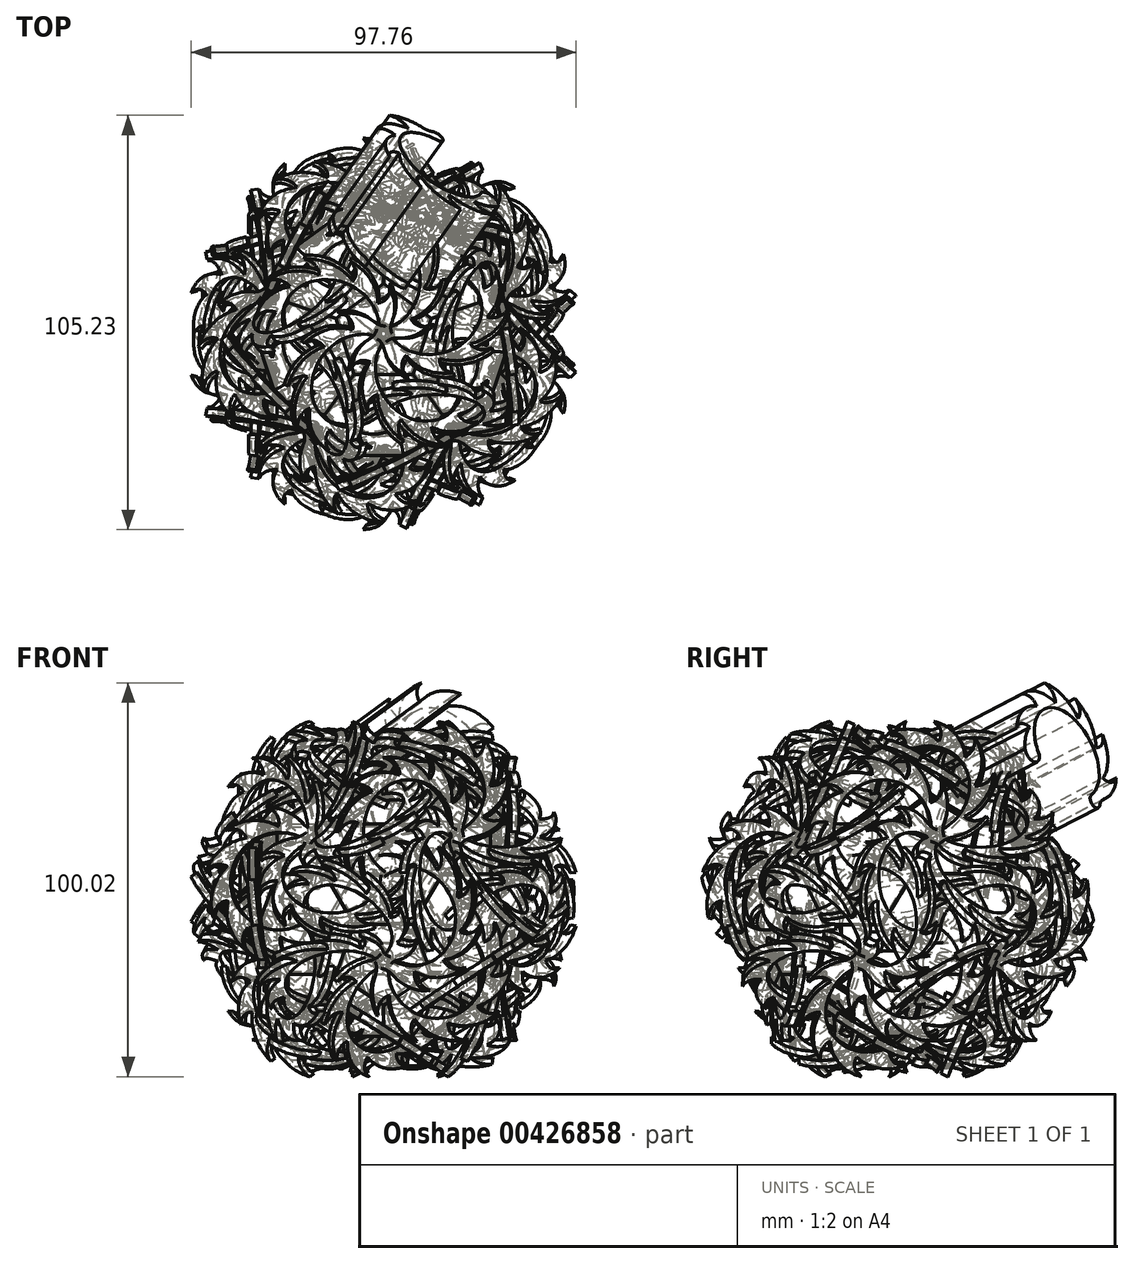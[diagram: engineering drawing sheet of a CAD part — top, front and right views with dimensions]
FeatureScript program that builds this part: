
annotation { "Feature Type Name" : "Feature", "Feature Type Description" : "" }
export const myFeature = defineFeature(function(context is Context, id is Id, definition is map)
    precondition{}
    {
        {
            var Q0;
            Q0=qCreatedBy(makeId("Top.planeOp"),FACE);
            var sketch = newSketch(context, id + "F0", { "sketchPlane" : qUnion([Q0])});
            skCircle(sketch, "E0.cCircle", {"center": v(0, 0) * mm, "radius": 10.32 * mm, "construction": true});
            skLineSegment(sketch, "E0.0", {"start": v(7.5, -10.32) * mm, "end": v(-7.5, -10.32) * mm});
            skLineSegment(sketch, "E0.1", {"start": v(-7.5, -10.32) * mm, "end": v(-12.14, 3.94) * mm});
            skLineSegment(sketch, "E0.2", {"start": v(-12.14, 3.94) * mm, "end": v(0, 12.76) * mm});
            skLineSegment(sketch, "E0.3", {"start": v(0, 12.76) * mm, "end": v(12.14, 3.94) * mm});
            skLineSegment(sketch, "E0.4", {"start": v(12.14, 3.94) * mm, "end": v(7.5, -10.32) * mm});
            skPoint(sketch, "E0.0.midPoint", {"position": v(0, -10.32) * mm});
            skLineSegment(sketch, "E1", {"start": v(0, 12.76) * mm, "end": v(0, -10.32) * mm});
            skSolve(sketch);
        }
        {
            var Q0;
            Q0=qCreatedBy(makeId("Top.planeOp"),FACE);
            var sketch = newSketch(context, id + "F1", { "sketchPlane" : qUnion([Q0])});
            skCircle(sketch, "E2.cCircle", {"center": v(22.17, -7.2) * mm, "radius": 13 * mm, "construction": true});
            skLineSegment(sketch, "E2.0", {"start": v(36.84, -4.09) * mm, "end": v(32.2, -18.35) * mm});
            skLineSegment(sketch, "E2.1", {"start": v(32.2, -18.35) * mm, "end": v(17.54, -21.47) * mm});
            skLineSegment(sketch, "E2.2", {"start": v(17.54, -21.47) * mm, "end": v(7.5, -10.32) * mm});
            skLineSegment(sketch, "E2.3", {"start": v(7.5, -10.32) * mm, "end": v(12.14, 3.94) * mm});
            skLineSegment(sketch, "E2.4", {"start": v(12.14, 3.94) * mm, "end": v(26.8, 7.06) * mm});
            skLineSegment(sketch, "E2.5", {"start": v(26.8, 7.06) * mm, "end": v(36.84, -4.09) * mm});
            skPoint(sketch, "E2.0.midPoint", {"position": v(34.53, -11.22) * mm});
            skSolve(sketch);
        }
        {
            var Q0;
            Q0=makeQuery(id+"F0.imprint","IMPRINT",FACE,{"disambiguationData":[TD([[makeQuery(id+"F0.imprint","IMPRINT",EDGE,{"derivedFrom":sQuery(id+"F0.wireOp",EDGE,"E0.0")}),-1.0]])]});
            extrude(context, id + "F2", {"entities" : qUnion([Q0]), "oppositeDirection" : true, "depth" : 1 * mm});
        }
        {
            var Q0;
            Q0=makeQuery(id+"F1.imprint","IMPRINT",FACE,{"disambiguationData":[TD([[makeQuery(id+"F1.imprint","IMPRINT",EDGE,{"derivedFrom":sQuery(id+"F1.wireOp",EDGE,"E2.0")}),-1.0]])]});
            extrude(context, id + "F3", {"entities" : qUnion([Q0]), "oppositeDirection" : true, "depth" : 1 * mm});
        }
        {
            var Q0;
            Q0=makeQuery(id+"F3.opExtrude","SWEPT_BODY",BODY,{"disambiguationData":[OSD([sQuery(id+"F1.wireOp",EDGE,"E2.0"),sQuery(id+"F1.wireOp",EDGE,"E2.1"),sQuery(id+"F1.wireOp",EDGE,"E2.2"),sQuery(id+"F1.wireOp",EDGE,"E2.3"),sQuery(id+"F1.wireOp",EDGE,"E2.4"),sQuery(id+"F1.wireOp",EDGE,"E2.5")])]});
            var Q1;
            Q1=makeQuery(id+"F2.opExtrude","CAP_EDGE",EDGE,{"disambiguationData":[OSD([sQuery(id+"F0.wireOp",EDGE,"E0.4")])],"isStart":true});
            transform(context, id + "F4", {"entities" : qUnion([Q0]), "transformType" : TransformType.ROTATION, "transformAxis" : qUnion([Q1]), "angle" : 37.38 * degree, "oppositeDirection" : true, "makeCopy" : false});
        }
        {
            var Q0;
            Q0=qCreatedBy(makeId("Right.planeOp"),FACE);
            var sketch = newSketch(context, id + "F5", { "sketchPlane" : qUnion([Q0])});
            skLineSegment(sketch, "E3", {"start": v(0, 0) * mm, "end": v(0, 7.73) * mm});
            skSolve(sketch);
        }
        {
            var Q0;
            Q0=makeQuery(id+"F3.opExtrude","SWEPT_BODY",BODY,{"disambiguationData":[OSD([sQuery(id+"F1.wireOp",EDGE,"E2.0"),sQuery(id+"F1.wireOp",EDGE,"E2.1"),sQuery(id+"F1.wireOp",EDGE,"E2.2"),sQuery(id+"F1.wireOp",EDGE,"E2.3"),sQuery(id+"F1.wireOp",EDGE,"E2.4"),sQuery(id+"F1.wireOp",EDGE,"E2.5")])]});
            var Q1;
            Q1=sQuery(id+"F5.wireOp",EDGE,"E3");
            circularPattern(context, id + "F6", {"entities" : qUnion([Q0]), "axis" : qUnion([Q1]), "angle" : 72 * degree, "instanceCount" : round(5)});
        }
        {
            var Q0;
            Q0=makeQuery(id+"F6.opPattern","COPY",FACE,{"derivedFrom":makeQuery(id+"F3.opExtrude","CAP_FACE",FACE,{"disambiguationData":[OSD([sQuery(id+"F1.wireOp",EDGE,"E2.0"),sQuery(id+"F1.wireOp",EDGE,"E2.1"),sQuery(id+"F1.wireOp",EDGE,"E2.2"),sQuery(id+"F1.wireOp",EDGE,"E2.3"),sQuery(id+"F1.wireOp",EDGE,"E2.4"),sQuery(id+"F1.wireOp",EDGE,"E2.5")])],"isStart":true}),"instanceName":"4"});
            var sketch = newSketch(context, id + "F7", { "sketchPlane" : qUnion([Q0])});
            skLineSegment(sketch, "E4", {"start": v(0, -34.18) * mm, "end": v(0, -8.2) * mm});
            skLineSegment(sketch, "E5", {"start": v(-15, -21.2) * mm, "end": v(15, -21.2) * mm});
            skCircle(sketch, "E6", {"center": v(0, -21.2) * mm, "radius": 3.24 * mm});
            skSolve(sketch);
        }
        {
            var Q0;
            Q0=qCreatedBy(makeId("Right.planeOp"),FACE);
            var sketch = newSketch(context, id + "F8", { "sketchPlane" : qUnion([Q0])});
            skArc(sketch, "E7.0", {"start": v(-1.37, 0) * mm, "mid": v(-18.04, 14.75) * mm, "end": v(-20.04, -7.42) * mm});
            skLineSegment(sketch, "E8", {"start": v(-20.04, -7.42) * mm, "end": v(-24.47, -10.8) * mm});
            skLineSegment(sketch, "E9", {"start": v(-1.37, 0) * mm, "end": v(0, 0) * mm});
            skArc(sketch, "E10", {"start": v(1.07, 1.27) * mm, "mid": v(3.46, 7.37) * mm, "end": v(2.5, 13.85) * mm});
            skArc(sketch, "E11", {"start": v(-0.8, 8.97) * mm, "mid": v(1.84, 10.74) * mm, "end": v(2.5, 13.85) * mm});
            skArc(sketch, "E12.1.0", {"start": v(-0.8, 8.97) * mm, "mid": v(-2.13, 15.94) * mm, "end": v(-6.98, 21.1) * mm});
            skArc(sketch, "E12.1.1", {"start": v(-6.75, 15.32) * mm, "mid": v(-5.72, 18.26) * mm, "end": v(-6.98, 21.1) * mm});
            skArc(sketch, "E12.2.0", {"start": v(-6.75, 15.32) * mm, "mid": v(-11.92, 20.18) * mm, "end": v(-18.89, 21.5) * mm});
            skArc(sketch, "E12.2.1", {"start": v(-15.3, 16.96) * mm, "mid": v(-16.2, 19.94) * mm, "end": v(-18.89, 21.5) * mm});
            skArc(sketch, "E12.3.0", {"start": v(-15.3, 16.96) * mm, "mid": v(-22.34, 17.85) * mm, "end": v(-28.75, 14.83) * mm});
            skArc(sketch, "E12.3.1", {"start": v(-23.18, 13.26) * mm, "mid": v(-25.66, 15.15) * mm, "end": v(-28.75, 14.83) * mm});
            skArc(sketch, "E12.4.0", {"start": v(-23.18, 13.26) * mm, "mid": v(-29.4, 9.84) * mm, "end": v(-32.81, 3.63) * mm});
            skArc(sketch, "E12.4.1", {"start": v(-27.38, 5.64) * mm, "mid": v(-30.5, 5.7) * mm, "end": v(-32.81, 3.63) * mm});
            skArc(sketch, "E12.5.0", {"start": v(-27.38, 5.64) * mm, "mid": v(-30.4, -0.78) * mm, "end": v(-29.51, -7.81) * mm});
            skArc(sketch, "E12.5.1", {"start": v(-26.3, -3) * mm, "mid": v(-28.86, -4.77) * mm, "end": v(-29.51, -7.81) * mm});
            skArc(sketch, "E12.6.0", {"start": v(-26.3, -3) * mm, "mid": v(-26.03, -7.06) * mm, "end": v(-24.49, -10.82) * mm});
            skArc(sketch, "E13", {"start": v(-24.49, -10.82) * mm, "mid": v(-20.56, -11.35) * mm, "end": v(-20.04, -7.42) * mm});
            skArc(sketch, "E14", {"start": v(-1.37, 0) * mm, "mid": v(1.27, -2.11) * mm, "end": v(1.07, 1.27) * mm});
            skSolve(sketch);
        }
        {
            var Q0;
            {var subQ2=sQuery(id+"F8.wireOp",EDGE,"E7.0");Q0=makeQuery(id+"F8.imprint","IMPRINT",FACE,{"disambiguationData":[TD([[makeQuery(id+"F8.imprint","IMPRINT",EDGE,{"derivedFrom":subQ2}),-1.0]])]});}
            extrude(context, id + "F9", {"entities" : qUnion([Q0]), "oppositeDirection" : true, "depth" : 2 * mm});
        }
        {
            var Q0;
            Q0=makeQuery(id+"F9.opExtrude","SWEPT_EDGE",EDGE,{"disambiguationData":[OSD([sQuery(id+"F8.wireOp",EDGE,"E10"),sQuery(id+"F8.wireOp",EDGE,"E14")])]});
            fillet(context, id + "F10", {"entities" : qUnion([Q0]), "radius" : 5 * mm, "tangentPropagation" : true, "allowEdgeOverflow" : false});
        }
        {
            var Q0;
            Q0=qCreatedBy(makeId("Right.planeOp"),FACE);
            var sketch = newSketch(context, id + "F11", { "sketchPlane" : qUnion([Q0])});
            skLineSegment(sketch, "E15", {"start": v(0, 0) * mm, "end": v(-20.65, -7.89) * mm});
            skLineSegment(sketch, "E16", {"start": v(0, 0) * mm, "end": v(0, 28.42) * mm});
            skSolve(sketch);
        }
        {
            var Q0;
            Q0=makeQuery(id+"F9.opExtrude","SWEPT_BODY",BODY,{"disambiguationData":[OSD([sQuery(id+"F8.wireOp",EDGE,"003f2e54-bd62-4f0b-a98e-8c36e71e2cf6"),sQuery(id+"F8.wireOp",EDGE,"8c729305-40a1-49fa-b790-4b99a3909bb6"),sQuery(id+"F8.wireOp",EDGE,"862a2a8f-3db7-4421-9c69-6ab2f53c4c24.1.0"),sQuery(id+"F8.wireOp",EDGE,"862a2a8f-3db7-4421-9c69-6ab2f53c4c24.1.1"),sQuery(id+"F8.wireOp",EDGE,"862a2a8f-3db7-4421-9c69-6ab2f53c4c24.2.0"),sQuery(id+"F8.wireOp",EDGE,"862a2a8f-3db7-4421-9c69-6ab2f53c4c24.2.1"),sQuery(id+"F8.wireOp",EDGE,"862a2a8f-3db7-4421-9c69-6ab2f53c4c24.3.0"),sQuery(id+"F8.wireOp",EDGE,"862a2a8f-3db7-4421-9c69-6ab2f53c4c24.3.1"),sQuery(id+"F8.wireOp",EDGE,"862a2a8f-3db7-4421-9c69-6ab2f53c4c24.4.0"),sQuery(id+"F8.wireOp",EDGE,"862a2a8f-3db7-4421-9c69-6ab2f53c4c24.4.1"),sQuery(id+"F8.wireOp",EDGE,"862a2a8f-3db7-4421-9c69-6ab2f53c4c24.5.0"),sQuery(id+"F8.wireOp",EDGE,"E7.0"),sQuery(id+"F8.wireOp",EDGE,"E8"),sQuery(id+"F8.wireOp",EDGE,"E9")])]});
            var Q1;
            Q1=sQuery(id+"F11.wireOp",EDGE,"E15");
            transform(context, id + "F12", {"entities" : qUnion([Q0]), "transformType" : TransformType.ROTATION, "transformAxis" : qUnion([Q1]), "angle" : 65 * degree, "makeCopy" : false});
        }
        {
            var Q0;
            Q0=makeQuery(id+"F9.opExtrude","SWEPT_BODY",BODY,{"disambiguationData":[OSD([sQuery(id+"F8.wireOp",EDGE,"003f2e54-bd62-4f0b-a98e-8c36e71e2cf6"),sQuery(id+"F8.wireOp",EDGE,"8c729305-40a1-49fa-b790-4b99a3909bb6"),sQuery(id+"F8.wireOp",EDGE,"862a2a8f-3db7-4421-9c69-6ab2f53c4c24.1.0"),sQuery(id+"F8.wireOp",EDGE,"862a2a8f-3db7-4421-9c69-6ab2f53c4c24.1.1"),sQuery(id+"F8.wireOp",EDGE,"862a2a8f-3db7-4421-9c69-6ab2f53c4c24.2.0"),sQuery(id+"F8.wireOp",EDGE,"862a2a8f-3db7-4421-9c69-6ab2f53c4c24.2.1"),sQuery(id+"F8.wireOp",EDGE,"862a2a8f-3db7-4421-9c69-6ab2f53c4c24.3.0"),sQuery(id+"F8.wireOp",EDGE,"862a2a8f-3db7-4421-9c69-6ab2f53c4c24.3.1"),sQuery(id+"F8.wireOp",EDGE,"862a2a8f-3db7-4421-9c69-6ab2f53c4c24.4.0"),sQuery(id+"F8.wireOp",EDGE,"862a2a8f-3db7-4421-9c69-6ab2f53c4c24.4.1"),sQuery(id+"F8.wireOp",EDGE,"862a2a8f-3db7-4421-9c69-6ab2f53c4c24.5.0"),sQuery(id+"F8.wireOp",EDGE,"E7.0"),sQuery(id+"F8.wireOp",EDGE,"E8"),sQuery(id+"F8.wireOp",EDGE,"E9")])]});
            var Q1;
            Q1=sQuery(id+"F11.wireOp",EDGE,"E16");
            circularPattern(context, id + "F13", {"entities" : qUnion([Q0]), "axis" : qUnion([Q1]), "angle" : 72 * degree, "instanceCount" : round(5)});
        }
        {
            var Q0;
            Q0=qCreatedBy(makeId("Right.planeOp"),FACE);
            var sketch = newSketch(context, id + "F14", { "sketchPlane" : qUnion([Q0])});
            skLineSegment(sketch, "E17.0", {"start": v(-30.97, -15.77) * mm, "end": v(-10.32, 0) * mm});
            skLineSegment(sketch, "E18", {"start": v(-20.65, -7.89) * mm, "end": v(-30.05, 4.42) * mm});
            skSolve(sketch);
        }
        {
            var Q0;
            Q0=makeQuery(id+"F9.opExtrude","SWEPT_BODY",BODY,{"disambiguationData":[OSD([sQuery(id+"F8.wireOp",EDGE,"003f2e54-bd62-4f0b-a98e-8c36e71e2cf6"),sQuery(id+"F8.wireOp",EDGE,"8c729305-40a1-49fa-b790-4b99a3909bb6"),sQuery(id+"F8.wireOp",EDGE,"862a2a8f-3db7-4421-9c69-6ab2f53c4c24.1.0"),sQuery(id+"F8.wireOp",EDGE,"862a2a8f-3db7-4421-9c69-6ab2f53c4c24.1.1"),sQuery(id+"F8.wireOp",EDGE,"862a2a8f-3db7-4421-9c69-6ab2f53c4c24.2.0"),sQuery(id+"F8.wireOp",EDGE,"862a2a8f-3db7-4421-9c69-6ab2f53c4c24.2.1"),sQuery(id+"F8.wireOp",EDGE,"862a2a8f-3db7-4421-9c69-6ab2f53c4c24.3.0"),sQuery(id+"F8.wireOp",EDGE,"862a2a8f-3db7-4421-9c69-6ab2f53c4c24.3.1"),sQuery(id+"F8.wireOp",EDGE,"862a2a8f-3db7-4421-9c69-6ab2f53c4c24.4.0"),sQuery(id+"F8.wireOp",EDGE,"862a2a8f-3db7-4421-9c69-6ab2f53c4c24.4.1"),sQuery(id+"F8.wireOp",EDGE,"862a2a8f-3db7-4421-9c69-6ab2f53c4c24.5.0"),sQuery(id+"F8.wireOp",EDGE,"E7.0"),sQuery(id+"F8.wireOp",EDGE,"E8"),sQuery(id+"F8.wireOp",EDGE,"E9")])]});
            var Q1;
            Q1=sQuery(id+"F14.wireOp",EDGE,"E18");
            circularPattern(context, id + "F15", {"entities" : qUnion([Q0]), "axis" : qUnion([Q1]), "angle" : 120 * degree, "instanceCount" : round(3)});
        }
        {
            var Q0;
            Q0=makeQuery(id+"F15.opPattern","COPY",BODY,{"derivedFrom":makeQuery(id+"F9.opExtrude","SWEPT_BODY",BODY,{"disambiguationData":[OSD([sQuery(id+"F8.wireOp",EDGE,"E7.0"),sQuery(id+"F8.wireOp",EDGE,"E10"),sQuery(id+"F8.wireOp",EDGE,"E11"),sQuery(id+"F8.wireOp",EDGE,"E12.1.0"),sQuery(id+"F8.wireOp",EDGE,"E12.1.1"),sQuery(id+"F8.wireOp",EDGE,"E12.2.0"),sQuery(id+"F8.wireOp",EDGE,"E12.2.1"),sQuery(id+"F8.wireOp",EDGE,"E12.3.0"),sQuery(id+"F8.wireOp",EDGE,"E12.3.1"),sQuery(id+"F8.wireOp",EDGE,"E12.4.0"),sQuery(id+"F8.wireOp",EDGE,"E12.4.1"),sQuery(id+"F8.wireOp",EDGE,"E12.5.0"),sQuery(id+"F8.wireOp",EDGE,"E12.5.1"),sQuery(id+"F8.wireOp",EDGE,"E12.6.0"),sQuery(id+"F8.wireOp",EDGE,"E13"),sQuery(id+"F8.wireOp",EDGE,"E14")])]}),"instanceName":"2"});
            var Q1;
            Q1=makeQuery(id+"F15.opPattern","COPY",BODY,{"derivedFrom":makeQuery(id+"F9.opExtrude","SWEPT_BODY",BODY,{"disambiguationData":[OSD([sQuery(id+"F8.wireOp",EDGE,"E7.0"),sQuery(id+"F8.wireOp",EDGE,"E10"),sQuery(id+"F8.wireOp",EDGE,"E11"),sQuery(id+"F8.wireOp",EDGE,"E12.1.0"),sQuery(id+"F8.wireOp",EDGE,"E12.1.1"),sQuery(id+"F8.wireOp",EDGE,"E12.2.0"),sQuery(id+"F8.wireOp",EDGE,"E12.2.1"),sQuery(id+"F8.wireOp",EDGE,"E12.3.0"),sQuery(id+"F8.wireOp",EDGE,"E12.3.1"),sQuery(id+"F8.wireOp",EDGE,"E12.4.0"),sQuery(id+"F8.wireOp",EDGE,"E12.4.1"),sQuery(id+"F8.wireOp",EDGE,"E12.5.0"),sQuery(id+"F8.wireOp",EDGE,"E12.5.1"),sQuery(id+"F8.wireOp",EDGE,"E12.6.0"),sQuery(id+"F8.wireOp",EDGE,"E13"),sQuery(id+"F8.wireOp",EDGE,"E14")])]}),"instanceName":"1"});
            var Q2;
            Q2=sQuery(id+"F11.wireOp",EDGE,"E16");
            circularPattern(context, id + "F16", {"entities" : qUnion([Q0, Q1]), "axis" : qUnion([Q2]), "angle" : 72 * degree, "instanceCount" : round(5)});
        }
        {
            var Q0;
            Q0=makeQuery(id+"F3.opExtrude","SWEPT_BODY",BODY,{"disambiguationData":[OSD([sQuery(id+"F1.wireOp",EDGE,"E2.0"),sQuery(id+"F1.wireOp",EDGE,"E2.1"),sQuery(id+"F1.wireOp",EDGE,"E2.2"),sQuery(id+"F1.wireOp",EDGE,"E2.3"),sQuery(id+"F1.wireOp",EDGE,"E2.4"),sQuery(id+"F1.wireOp",EDGE,"E2.5")])]});
            var Q1;
            Q1=makeQuery(id+"F16.opPattern","COPY",BODY,{"derivedFrom":makeQuery(id+"F15.opPattern","COPY",BODY,{"derivedFrom":makeQuery(id+"F9.opExtrude","SWEPT_BODY",BODY,{"disambiguationData":[OSD([sQuery(id+"F8.wireOp",EDGE,"E7.0"),sQuery(id+"F8.wireOp",EDGE,"E10"),sQuery(id+"F8.wireOp",EDGE,"E11"),sQuery(id+"F8.wireOp",EDGE,"E12.1.0"),sQuery(id+"F8.wireOp",EDGE,"E12.1.1"),sQuery(id+"F8.wireOp",EDGE,"E12.2.0"),sQuery(id+"F8.wireOp",EDGE,"E12.2.1"),sQuery(id+"F8.wireOp",EDGE,"E12.3.0"),sQuery(id+"F8.wireOp",EDGE,"E12.3.1"),sQuery(id+"F8.wireOp",EDGE,"E12.4.0"),sQuery(id+"F8.wireOp",EDGE,"E12.4.1"),sQuery(id+"F8.wireOp",EDGE,"E12.5.0"),sQuery(id+"F8.wireOp",EDGE,"E12.5.1"),sQuery(id+"F8.wireOp",EDGE,"E12.6.0"),sQuery(id+"F8.wireOp",EDGE,"E13"),sQuery(id+"F8.wireOp",EDGE,"E14")])]}),"instanceName":"1"}),"instanceName":"1"});
            var Q2;
            Q2=makeQuery(id+"F13.opPattern","COPY",BODY,{"derivedFrom":makeQuery(id+"F9.opExtrude","SWEPT_BODY",BODY,{"disambiguationData":[OSD([sQuery(id+"F8.wireOp",EDGE,"E7.0"),sQuery(id+"F8.wireOp",EDGE,"E10"),sQuery(id+"F8.wireOp",EDGE,"E11"),sQuery(id+"F8.wireOp",EDGE,"E12.1.0"),sQuery(id+"F8.wireOp",EDGE,"E12.1.1"),sQuery(id+"F8.wireOp",EDGE,"E12.2.0"),sQuery(id+"F8.wireOp",EDGE,"E12.2.1"),sQuery(id+"F8.wireOp",EDGE,"E12.3.0"),sQuery(id+"F8.wireOp",EDGE,"E12.3.1"),sQuery(id+"F8.wireOp",EDGE,"E12.4.0"),sQuery(id+"F8.wireOp",EDGE,"E12.4.1"),sQuery(id+"F8.wireOp",EDGE,"E12.5.0"),sQuery(id+"F8.wireOp",EDGE,"E12.5.1"),sQuery(id+"F8.wireOp",EDGE,"E12.6.0"),sQuery(id+"F8.wireOp",EDGE,"E13"),sQuery(id+"F8.wireOp",EDGE,"E14")])]}),"instanceName":"1"});
            var Q3;
            Q3=makeQuery(id+"F16.opPattern","COPY",BODY,{"derivedFrom":makeQuery(id+"F15.opPattern","COPY",BODY,{"derivedFrom":makeQuery(id+"F9.opExtrude","SWEPT_BODY",BODY,{"disambiguationData":[OSD([sQuery(id+"F8.wireOp",EDGE,"E7.0"),sQuery(id+"F8.wireOp",EDGE,"E10"),sQuery(id+"F8.wireOp",EDGE,"E11"),sQuery(id+"F8.wireOp",EDGE,"E12.1.0"),sQuery(id+"F8.wireOp",EDGE,"E12.1.1"),sQuery(id+"F8.wireOp",EDGE,"E12.2.0"),sQuery(id+"F8.wireOp",EDGE,"E12.2.1"),sQuery(id+"F8.wireOp",EDGE,"E12.3.0"),sQuery(id+"F8.wireOp",EDGE,"E12.3.1"),sQuery(id+"F8.wireOp",EDGE,"E12.4.0"),sQuery(id+"F8.wireOp",EDGE,"E12.4.1"),sQuery(id+"F8.wireOp",EDGE,"E12.5.0"),sQuery(id+"F8.wireOp",EDGE,"E12.5.1"),sQuery(id+"F8.wireOp",EDGE,"E12.6.0"),sQuery(id+"F8.wireOp",EDGE,"E13"),sQuery(id+"F8.wireOp",EDGE,"E14")])]}),"instanceName":"2"}),"instanceName":"1"});
            var Q4;
            Q4=sQuery(id+"F14.wireOp",EDGE,"E18");
            circularPattern(context, id + "F17", {"entities" : qUnion([Q0, Q1, Q2, Q3]), "axis" : qUnion([Q4]), "angle" : 120 * degree, "instanceCount" : 2, "oppositeDirection" : true});
        }
        {
            var Q0;
            Q0=makeQuery(id+"F2.opExtrude","SWEPT_BODY",BODY,{"disambiguationData":[OSD([sQuery(id+"F0.wireOp",EDGE,"E0.0"),sQuery(id+"F0.wireOp",EDGE,"E0.1"),sQuery(id+"F0.wireOp",EDGE,"E0.2"),sQuery(id+"F0.wireOp",EDGE,"E0.3"),sQuery(id+"F0.wireOp",EDGE,"E0.4")])]});
            var Q1;
            Q1=makeQuery(id+"F13.opPattern","COPY",BODY,{"derivedFrom":makeQuery(id+"F9.opExtrude","SWEPT_BODY",BODY,{"disambiguationData":[OSD([sQuery(id+"F8.wireOp",EDGE,"E7.0"),sQuery(id+"F8.wireOp",EDGE,"E10"),sQuery(id+"F8.wireOp",EDGE,"E11"),sQuery(id+"F8.wireOp",EDGE,"E12.1.0"),sQuery(id+"F8.wireOp",EDGE,"E12.1.1"),sQuery(id+"F8.wireOp",EDGE,"E12.2.0"),sQuery(id+"F8.wireOp",EDGE,"E12.2.1"),sQuery(id+"F8.wireOp",EDGE,"E12.3.0"),sQuery(id+"F8.wireOp",EDGE,"E12.3.1"),sQuery(id+"F8.wireOp",EDGE,"E12.4.0"),sQuery(id+"F8.wireOp",EDGE,"E12.4.1"),sQuery(id+"F8.wireOp",EDGE,"E12.5.0"),sQuery(id+"F8.wireOp",EDGE,"E12.5.1"),sQuery(id+"F8.wireOp",EDGE,"E12.6.0"),sQuery(id+"F8.wireOp",EDGE,"E13"),sQuery(id+"F8.wireOp",EDGE,"E14")])]}),"instanceName":"2"});
            var Q2;
            Q2=makeQuery(id+"F13.opPattern","COPY",BODY,{"derivedFrom":makeQuery(id+"F9.opExtrude","SWEPT_BODY",BODY,{"disambiguationData":[OSD([sQuery(id+"F8.wireOp",EDGE,"E7.0"),sQuery(id+"F8.wireOp",EDGE,"E10"),sQuery(id+"F8.wireOp",EDGE,"E11"),sQuery(id+"F8.wireOp",EDGE,"E12.1.0"),sQuery(id+"F8.wireOp",EDGE,"E12.1.1"),sQuery(id+"F8.wireOp",EDGE,"E12.2.0"),sQuery(id+"F8.wireOp",EDGE,"E12.2.1"),sQuery(id+"F8.wireOp",EDGE,"E12.3.0"),sQuery(id+"F8.wireOp",EDGE,"E12.3.1"),sQuery(id+"F8.wireOp",EDGE,"E12.4.0"),sQuery(id+"F8.wireOp",EDGE,"E12.4.1"),sQuery(id+"F8.wireOp",EDGE,"E12.5.0"),sQuery(id+"F8.wireOp",EDGE,"E12.5.1"),sQuery(id+"F8.wireOp",EDGE,"E12.6.0"),sQuery(id+"F8.wireOp",EDGE,"E13"),sQuery(id+"F8.wireOp",EDGE,"E14")])]}),"instanceName":"3"});
            var Q3;
            Q3=sQuery(id+"F14.wireOp",EDGE,"E18");
            circularPattern(context, id + "F18", {"entities" : qUnion([Q0, Q1, Q2]), "axis" : qUnion([Q3]), "angle" : 120 * degree, "instanceCount" : round(3)});
        }
        {
            var Q0;
            Q0=makeQuery(id+"F18.opPattern","COPY",FACE,{"derivedFrom":makeQuery(id+"F2.opExtrude","CAP_FACE",FACE,{"disambiguationData":[OSD([sQuery(id+"F0.wireOp",EDGE,"E0.0"),sQuery(id+"F0.wireOp",EDGE,"E0.1"),sQuery(id+"F0.wireOp",EDGE,"E0.2"),sQuery(id+"F0.wireOp",EDGE,"E0.3"),sQuery(id+"F0.wireOp",EDGE,"E0.4")])],"isStart":true}),"instanceName":"1"});
            var sketch = newSketch(context, id + "F19", { "sketchPlane" : qUnion([Q0])});
            skLineSegment(sketch, "E19", {"start": v(-1.3, -23.63) * mm, "end": v(-19.97, -37.2) * mm});
            skLineSegment(sketch, "E20", {"start": v(-19.97, -22.2) * mm, "end": v(-1.3, -35.77) * mm});
            skSolve(sketch);
        }
        {
            var Q0;
            Q0=sQuery(id+"F19.wireOp",VERTEX,"E19.end");
            var Q1;
            Q1=sQuery(id+"F19.wireOp",VERTEX,"E19.start");
            var Q2;
            Q2=sQuery(id+"F14.wireOp",VERTEX,"E18.end");
            cPlane(context, id + "F20", {"entities" : qUnion([Q0, Q1, Q2]), "cplaneType" : CPlaneType.THREE_POINT, "offset" : 150 * mm, "width" : 150 * mm, "height" : 150 * mm});
        }
        {
            var Q0;
            Q0=qCreatedBy(id+"F20.planeOp",FACE);
            var sketch = newSketch(context, id + "F21", { "sketchPlane" : qUnion([Q0])});
            skLineSegment(sketch, "E21.0", {"start": v(23.59, 6.27) * mm, "end": v(41.93, -7.75) * mm});
            skLineSegment(sketch, "E21.1", {"start": v(34.92, -2.4) * mm, "end": v(29.26, 1.94) * mm});
            skLineSegment(sketch, "E22", {"start": v(31.8, 0) * mm, "end": v(33.22, 1.87) * mm});
            skLineSegment(sketch, "E23", {"start": v(33.22, 1.87) * mm, "end": v(37.58, 7.58) * mm});
            skSolve(sketch);
        }
        {
            var Q0;
            Q0=makeQuery(id+"F17.opPattern","COPY",BODY,{"derivedFrom":makeQuery(id+"F3.opExtrude","SWEPT_BODY",BODY,{"disambiguationData":[OSD([sQuery(id+"F1.wireOp",EDGE,"E2.0"),sQuery(id+"F1.wireOp",EDGE,"E2.1"),sQuery(id+"F1.wireOp",EDGE,"E2.2"),sQuery(id+"F1.wireOp",EDGE,"E2.3"),sQuery(id+"F1.wireOp",EDGE,"E2.4"),sQuery(id+"F1.wireOp",EDGE,"E2.5")])]}),"instanceName":"1"});
            var Q1;
            Q1=makeQuery(id+"F17.opPattern","COPY",BODY,{"derivedFrom":makeQuery(id+"F13.opPattern","COPY",BODY,{"derivedFrom":makeQuery(id+"F9.opExtrude","SWEPT_BODY",BODY,{"disambiguationData":[OSD([sQuery(id+"F8.wireOp",EDGE,"E7.0"),sQuery(id+"F8.wireOp",EDGE,"E10"),sQuery(id+"F8.wireOp",EDGE,"E11"),sQuery(id+"F8.wireOp",EDGE,"E12.1.0"),sQuery(id+"F8.wireOp",EDGE,"E12.1.1"),sQuery(id+"F8.wireOp",EDGE,"E12.2.0"),sQuery(id+"F8.wireOp",EDGE,"E12.2.1"),sQuery(id+"F8.wireOp",EDGE,"E12.3.0"),sQuery(id+"F8.wireOp",EDGE,"E12.3.1"),sQuery(id+"F8.wireOp",EDGE,"E12.4.0"),sQuery(id+"F8.wireOp",EDGE,"E12.4.1"),sQuery(id+"F8.wireOp",EDGE,"E12.5.0"),sQuery(id+"F8.wireOp",EDGE,"E12.5.1"),sQuery(id+"F8.wireOp",EDGE,"E12.6.0"),sQuery(id+"F8.wireOp",EDGE,"E13"),sQuery(id+"F8.wireOp",EDGE,"E14")])]}),"instanceName":"1"}),"instanceName":"1"});
            var Q2;
            Q2=makeQuery(id+"F17.opPattern","COPY",BODY,{"derivedFrom":makeQuery(id+"F16.opPattern","COPY",BODY,{"derivedFrom":makeQuery(id+"F15.opPattern","COPY",BODY,{"derivedFrom":makeQuery(id+"F9.opExtrude","SWEPT_BODY",BODY,{"disambiguationData":[OSD([sQuery(id+"F8.wireOp",EDGE,"E7.0"),sQuery(id+"F8.wireOp",EDGE,"E10"),sQuery(id+"F8.wireOp",EDGE,"E11"),sQuery(id+"F8.wireOp",EDGE,"E12.1.0"),sQuery(id+"F8.wireOp",EDGE,"E12.1.1"),sQuery(id+"F8.wireOp",EDGE,"E12.2.0"),sQuery(id+"F8.wireOp",EDGE,"E12.2.1"),sQuery(id+"F8.wireOp",EDGE,"E12.3.0"),sQuery(id+"F8.wireOp",EDGE,"E12.3.1"),sQuery(id+"F8.wireOp",EDGE,"E12.4.0"),sQuery(id+"F8.wireOp",EDGE,"E12.4.1"),sQuery(id+"F8.wireOp",EDGE,"E12.5.0"),sQuery(id+"F8.wireOp",EDGE,"E12.5.1"),sQuery(id+"F8.wireOp",EDGE,"E12.6.0"),sQuery(id+"F8.wireOp",EDGE,"E13"),sQuery(id+"F8.wireOp",EDGE,"E14")])]}),"instanceName":"2"}),"instanceName":"1"}),"instanceName":"1"});
            var Q3;
            Q3=makeQuery(id+"F17.opPattern","COPY",BODY,{"derivedFrom":makeQuery(id+"F16.opPattern","COPY",BODY,{"derivedFrom":makeQuery(id+"F15.opPattern","COPY",BODY,{"derivedFrom":makeQuery(id+"F9.opExtrude","SWEPT_BODY",BODY,{"disambiguationData":[OSD([sQuery(id+"F8.wireOp",EDGE,"E7.0"),sQuery(id+"F8.wireOp",EDGE,"E10"),sQuery(id+"F8.wireOp",EDGE,"E11"),sQuery(id+"F8.wireOp",EDGE,"E12.1.0"),sQuery(id+"F8.wireOp",EDGE,"E12.1.1"),sQuery(id+"F8.wireOp",EDGE,"E12.2.0"),sQuery(id+"F8.wireOp",EDGE,"E12.2.1"),sQuery(id+"F8.wireOp",EDGE,"E12.3.0"),sQuery(id+"F8.wireOp",EDGE,"E12.3.1"),sQuery(id+"F8.wireOp",EDGE,"E12.4.0"),sQuery(id+"F8.wireOp",EDGE,"E12.4.1"),sQuery(id+"F8.wireOp",EDGE,"E12.5.0"),sQuery(id+"F8.wireOp",EDGE,"E12.5.1"),sQuery(id+"F8.wireOp",EDGE,"E12.6.0"),sQuery(id+"F8.wireOp",EDGE,"E13"),sQuery(id+"F8.wireOp",EDGE,"E14")])]}),"instanceName":"1"}),"instanceName":"1"}),"instanceName":"1"});
            var Q4;
            Q4=sQuery(id+"F21.wireOp",EDGE,"E22");
            circularPattern(context, id + "F22", {"entities" : qUnion([Q0, Q1, Q2, Q3]), "axis" : qUnion([Q4]), "angle" : 72 * degree, "instanceCount" : round(3), "oppositeDirection" : true});
        }
        {
            var Q0;
            Q0=makeQuery(id+"F18.opPattern","COPY",FACE,{"derivedFrom":makeQuery(id+"F2.opExtrude","CAP_FACE",FACE,{"disambiguationData":[OSD([sQuery(id+"F0.wireOp",EDGE,"E0.0"),sQuery(id+"F0.wireOp",EDGE,"E0.1"),sQuery(id+"F0.wireOp",EDGE,"E0.2"),sQuery(id+"F0.wireOp",EDGE,"E0.3"),sQuery(id+"F0.wireOp",EDGE,"E0.4")])],"isStart":true}),"instanceName":"2"});
            var sketch = newSketch(context, id + "F23", { "sketchPlane" : qUnion([Q0])});
            skLineSegment(sketch, "E24", {"start": v(1.3, -23.63) * mm, "end": v(19.97, -37.2) * mm});
            skLineSegment(sketch, "E25", {"start": v(5.7, -41.83) * mm, "end": v(12.84, -19.88) * mm});
            skSolve(sketch);
        }
        {
            var Q0;
            Q0=sQuery(id+"F23.wireOp",VERTEX,"E24.end");
            var Q1;
            Q1=sQuery(id+"F23.wireOp",VERTEX,"E24.start");
            var Q2;
            Q2=sQuery(id+"F14.wireOp",VERTEX,"E18.end");
            cPlane(context, id + "F24", {"entities" : qUnion([Q0, Q1, Q2]), "cplaneType" : CPlaneType.THREE_POINT, "offset" : 150 * mm, "width" : 150 * mm, "height" : 150 * mm});
        }
        {
            var Q0;
            Q0=qCreatedBy(id+"F24.planeOp",FACE);
            var sketch = newSketch(context, id + "F25", { "sketchPlane" : qUnion([Q0])});
            skLineSegment(sketch, "E26.0", {"start": v(23.59, 6.27) * mm, "end": v(41.93, -7.75) * mm});
            skLineSegment(sketch, "E26.1", {"start": v(34.92, -2.4) * mm, "end": v(29.26, 1.94) * mm});
            skLineSegment(sketch, "E27", {"start": v(31.8, 0) * mm, "end": v(36.23, 5.8) * mm});
            skSolve(sketch);
        }
        {
            var Q0;
            Q0=makeQuery(id+"F3.opExtrude","SWEPT_BODY",BODY,{"disambiguationData":[OSD([sQuery(id+"F1.wireOp",EDGE,"E2.0"),sQuery(id+"F1.wireOp",EDGE,"E2.1"),sQuery(id+"F1.wireOp",EDGE,"E2.2"),sQuery(id+"F1.wireOp",EDGE,"E2.3"),sQuery(id+"F1.wireOp",EDGE,"E2.4"),sQuery(id+"F1.wireOp",EDGE,"E2.5")])]});
            var Q1;
            Q1=makeQuery(id+"F16.opPattern","COPY",BODY,{"derivedFrom":makeQuery(id+"F15.opPattern","COPY",BODY,{"derivedFrom":makeQuery(id+"F9.opExtrude","SWEPT_BODY",BODY,{"disambiguationData":[OSD([sQuery(id+"F8.wireOp",EDGE,"E7.0"),sQuery(id+"F8.wireOp",EDGE,"E10"),sQuery(id+"F8.wireOp",EDGE,"E11"),sQuery(id+"F8.wireOp",EDGE,"E12.1.0"),sQuery(id+"F8.wireOp",EDGE,"E12.1.1"),sQuery(id+"F8.wireOp",EDGE,"E12.2.0"),sQuery(id+"F8.wireOp",EDGE,"E12.2.1"),sQuery(id+"F8.wireOp",EDGE,"E12.3.0"),sQuery(id+"F8.wireOp",EDGE,"E12.3.1"),sQuery(id+"F8.wireOp",EDGE,"E12.4.0"),sQuery(id+"F8.wireOp",EDGE,"E12.4.1"),sQuery(id+"F8.wireOp",EDGE,"E12.5.0"),sQuery(id+"F8.wireOp",EDGE,"E12.5.1"),sQuery(id+"F8.wireOp",EDGE,"E12.6.0"),sQuery(id+"F8.wireOp",EDGE,"E13"),sQuery(id+"F8.wireOp",EDGE,"E14")])]}),"instanceName":"2"}),"instanceName":"1"});
            var Q2;
            Q2=makeQuery(id+"F13.opPattern","COPY",BODY,{"derivedFrom":makeQuery(id+"F9.opExtrude","SWEPT_BODY",BODY,{"disambiguationData":[OSD([sQuery(id+"F8.wireOp",EDGE,"E7.0"),sQuery(id+"F8.wireOp",EDGE,"E10"),sQuery(id+"F8.wireOp",EDGE,"E11"),sQuery(id+"F8.wireOp",EDGE,"E12.1.0"),sQuery(id+"F8.wireOp",EDGE,"E12.1.1"),sQuery(id+"F8.wireOp",EDGE,"E12.2.0"),sQuery(id+"F8.wireOp",EDGE,"E12.2.1"),sQuery(id+"F8.wireOp",EDGE,"E12.3.0"),sQuery(id+"F8.wireOp",EDGE,"E12.3.1"),sQuery(id+"F8.wireOp",EDGE,"E12.4.0"),sQuery(id+"F8.wireOp",EDGE,"E12.4.1"),sQuery(id+"F8.wireOp",EDGE,"E12.5.0"),sQuery(id+"F8.wireOp",EDGE,"E12.5.1"),sQuery(id+"F8.wireOp",EDGE,"E12.6.0"),sQuery(id+"F8.wireOp",EDGE,"E13"),sQuery(id+"F8.wireOp",EDGE,"E14")])]}),"instanceName":"1"});
            var Q3;
            Q3=makeQuery(id+"F16.opPattern","COPY",BODY,{"derivedFrom":makeQuery(id+"F15.opPattern","COPY",BODY,{"derivedFrom":makeQuery(id+"F9.opExtrude","SWEPT_BODY",BODY,{"disambiguationData":[OSD([sQuery(id+"F8.wireOp",EDGE,"E7.0"),sQuery(id+"F8.wireOp",EDGE,"E10"),sQuery(id+"F8.wireOp",EDGE,"E11"),sQuery(id+"F8.wireOp",EDGE,"E12.1.0"),sQuery(id+"F8.wireOp",EDGE,"E12.1.1"),sQuery(id+"F8.wireOp",EDGE,"E12.2.0"),sQuery(id+"F8.wireOp",EDGE,"E12.2.1"),sQuery(id+"F8.wireOp",EDGE,"E12.3.0"),sQuery(id+"F8.wireOp",EDGE,"E12.3.1"),sQuery(id+"F8.wireOp",EDGE,"E12.4.0"),sQuery(id+"F8.wireOp",EDGE,"E12.4.1"),sQuery(id+"F8.wireOp",EDGE,"E12.5.0"),sQuery(id+"F8.wireOp",EDGE,"E12.5.1"),sQuery(id+"F8.wireOp",EDGE,"E12.6.0"),sQuery(id+"F8.wireOp",EDGE,"E13"),sQuery(id+"F8.wireOp",EDGE,"E14")])]}),"instanceName":"1"}),"instanceName":"1"});
            var Q4;
            Q4=sQuery(id+"F25.wireOp",EDGE,"E27");
            circularPattern(context, id + "F26", {"entities" : qUnion([Q0, Q1, Q2, Q3]), "axis" : qUnion([Q4]), "angle" : 72 * degree, "instanceCount" : round(3), "oppositeDirection" : true});
        }
        {
            var Q0;
            Q0=makeQuery(id+"F17.opPattern","COPY",FACE,{"derivedFrom":makeQuery(id+"F3.opExtrude","CAP_FACE",FACE,{"disambiguationData":[OSD([sQuery(id+"F1.wireOp",EDGE,"E2.0"),sQuery(id+"F1.wireOp",EDGE,"E2.1"),sQuery(id+"F1.wireOp",EDGE,"E2.2"),sQuery(id+"F1.wireOp",EDGE,"E2.3"),sQuery(id+"F1.wireOp",EDGE,"E2.4"),sQuery(id+"F1.wireOp",EDGE,"E2.5")])],"isStart":true}),"instanceName":"1"});
            var sketch = newSketch(context, id + "F27", { "sketchPlane" : qUnion([Q0])});
            skLineSegment(sketch, "E28", {"start": v(0, -47.28) * mm, "end": v(0, -21.3) * mm});
            skSolve(sketch);
        }
        {
            var Q0;
            Q0=qCreatedBy(makeId("Right.planeOp"),FACE);
            var sketch = newSketch(context, id + "F28", { "sketchPlane" : qUnion([Q0])});
            skLineSegment(sketch, "E29.0", {"start": v(-35.84, -41.3) * mm, "end": v(-30.97, -15.77) * mm});
            skLineSegment(sketch, "E30", {"start": v(-33.4, -28.53) * mm, "end": v(-47.6, -25.82) * mm});
            skSolve(sketch);
        }
        {
            var Q0;
            Q0=makeQuery(id+"F18.opPattern","COPY",BODY,{"derivedFrom":makeQuery(id+"F2.opExtrude","SWEPT_BODY",BODY,{"disambiguationData":[OSD([sQuery(id+"F0.wireOp",EDGE,"E0.0"),sQuery(id+"F0.wireOp",EDGE,"E0.1"),sQuery(id+"F0.wireOp",EDGE,"E0.2"),sQuery(id+"F0.wireOp",EDGE,"E0.3"),sQuery(id+"F0.wireOp",EDGE,"E0.4")])]}),"instanceName":"2"});
            var Q1;
            Q1=sQuery(id+"F28.wireOp",EDGE,"E30");
            circularPattern(context, id + "F29", {"entities" : qUnion([Q0]), "axis" : qUnion([Q1]), "angle" : 120 * degree, "instanceCount" : 2, "oppositeDirection" : true});
        }
        {
            var Q0;
            Q0=makeQuery(id+"F29.opPattern","COPY",FACE,{"derivedFrom":makeQuery(id+"F18.opPattern","COPY",FACE,{"derivedFrom":makeQuery(id+"F2.opExtrude","CAP_FACE",FACE,{"disambiguationData":[OSD([sQuery(id+"F0.wireOp",EDGE,"E0.0"),sQuery(id+"F0.wireOp",EDGE,"E0.1"),sQuery(id+"F0.wireOp",EDGE,"E0.2"),sQuery(id+"F0.wireOp",EDGE,"E0.3"),sQuery(id+"F0.wireOp",EDGE,"E0.4")])],"isStart":true}),"instanceName":"2"}),"instanceName":"1"});
            var sketch = newSketch(context, id + "F30", { "sketchPlane" : qUnion([Q0])});
            skLineSegment(sketch, "E31", {"start": v(0, -43.99) * mm, "end": v(0, -31.23) * mm});
            skLineSegment(sketch, "E32", {"start": v(-12.14, -35.17) * mm, "end": v(9.82, -28.04) * mm});
            skPoint(sketch, "E33.orphan", {"position": v(0, -20.9) * mm});
            skSolve(sketch);
        }
        {
            var Q0;
            Q0=qCreatedBy(makeId("Right.planeOp"),FACE);
            var sketch = newSketch(context, id + "F31", { "sketchPlane" : qUnion([Q0])});
            skLineSegment(sketch, "E34.0", {"start": v(-25.52, -61.94) * mm, "end": v(-31.23, -50.52) * mm});
            skLineSegment(sketch, "E35", {"start": v(-31.23, -50.52) * mm, "end": v(-51.07, -60.45) * mm});
            skSolve(sketch);
        }
        {
            var Q0;
            Q0=makeQuery(id+"F26.opPattern","COPY",BODY,{"derivedFrom":makeQuery(id+"F3.opExtrude","SWEPT_BODY",BODY,{"disambiguationData":[OSD([sQuery(id+"F1.wireOp",EDGE,"E2.0"),sQuery(id+"F1.wireOp",EDGE,"E2.1"),sQuery(id+"F1.wireOp",EDGE,"E2.2"),sQuery(id+"F1.wireOp",EDGE,"E2.3"),sQuery(id+"F1.wireOp",EDGE,"E2.4"),sQuery(id+"F1.wireOp",EDGE,"E2.5")])]}),"instanceName":"2"});
            var Q1;
            Q1=makeQuery(id+"F26.opPattern","COPY",BODY,{"derivedFrom":makeQuery(id+"F16.opPattern","COPY",BODY,{"derivedFrom":makeQuery(id+"F15.opPattern","COPY",BODY,{"derivedFrom":makeQuery(id+"F9.opExtrude","SWEPT_BODY",BODY,{"disambiguationData":[OSD([sQuery(id+"F8.wireOp",EDGE,"E7.0"),sQuery(id+"F8.wireOp",EDGE,"E10"),sQuery(id+"F8.wireOp",EDGE,"E11"),sQuery(id+"F8.wireOp",EDGE,"E12.1.0"),sQuery(id+"F8.wireOp",EDGE,"E12.1.1"),sQuery(id+"F8.wireOp",EDGE,"E12.2.0"),sQuery(id+"F8.wireOp",EDGE,"E12.2.1"),sQuery(id+"F8.wireOp",EDGE,"E12.3.0"),sQuery(id+"F8.wireOp",EDGE,"E12.3.1"),sQuery(id+"F8.wireOp",EDGE,"E12.4.0"),sQuery(id+"F8.wireOp",EDGE,"E12.4.1"),sQuery(id+"F8.wireOp",EDGE,"E12.5.0"),sQuery(id+"F8.wireOp",EDGE,"E12.5.1"),sQuery(id+"F8.wireOp",EDGE,"E12.6.0"),sQuery(id+"F8.wireOp",EDGE,"E13"),sQuery(id+"F8.wireOp",EDGE,"E14")])]}),"instanceName":"2"}),"instanceName":"1"}),"instanceName":"2"});
            var Q2;
            Q2=makeQuery(id+"F26.opPattern","COPY",BODY,{"derivedFrom":makeQuery(id+"F13.opPattern","COPY",BODY,{"derivedFrom":makeQuery(id+"F9.opExtrude","SWEPT_BODY",BODY,{"disambiguationData":[OSD([sQuery(id+"F8.wireOp",EDGE,"E7.0"),sQuery(id+"F8.wireOp",EDGE,"E10"),sQuery(id+"F8.wireOp",EDGE,"E11"),sQuery(id+"F8.wireOp",EDGE,"E12.1.0"),sQuery(id+"F8.wireOp",EDGE,"E12.1.1"),sQuery(id+"F8.wireOp",EDGE,"E12.2.0"),sQuery(id+"F8.wireOp",EDGE,"E12.2.1"),sQuery(id+"F8.wireOp",EDGE,"E12.3.0"),sQuery(id+"F8.wireOp",EDGE,"E12.3.1"),sQuery(id+"F8.wireOp",EDGE,"E12.4.0"),sQuery(id+"F8.wireOp",EDGE,"E12.4.1"),sQuery(id+"F8.wireOp",EDGE,"E12.5.0"),sQuery(id+"F8.wireOp",EDGE,"E12.5.1"),sQuery(id+"F8.wireOp",EDGE,"E12.6.0"),sQuery(id+"F8.wireOp",EDGE,"E13"),sQuery(id+"F8.wireOp",EDGE,"E14")])]}),"instanceName":"1"}),"instanceName":"2"});
            var Q3;
            Q3=makeQuery(id+"F18.opPattern","COPY",BODY,{"derivedFrom":makeQuery(id+"F13.opPattern","COPY",BODY,{"derivedFrom":makeQuery(id+"F9.opExtrude","SWEPT_BODY",BODY,{"disambiguationData":[OSD([sQuery(id+"F8.wireOp",EDGE,"E7.0"),sQuery(id+"F8.wireOp",EDGE,"E10"),sQuery(id+"F8.wireOp",EDGE,"E11"),sQuery(id+"F8.wireOp",EDGE,"E12.1.0"),sQuery(id+"F8.wireOp",EDGE,"E12.1.1"),sQuery(id+"F8.wireOp",EDGE,"E12.2.0"),sQuery(id+"F8.wireOp",EDGE,"E12.2.1"),sQuery(id+"F8.wireOp",EDGE,"E12.3.0"),sQuery(id+"F8.wireOp",EDGE,"E12.3.1"),sQuery(id+"F8.wireOp",EDGE,"E12.4.0"),sQuery(id+"F8.wireOp",EDGE,"E12.4.1"),sQuery(id+"F8.wireOp",EDGE,"E12.5.0"),sQuery(id+"F8.wireOp",EDGE,"E12.5.1"),sQuery(id+"F8.wireOp",EDGE,"E12.6.0"),sQuery(id+"F8.wireOp",EDGE,"E13"),sQuery(id+"F8.wireOp",EDGE,"E14")])]}),"instanceName":"2"}),"instanceName":"2"});
            var Q4;
            Q4=sQuery(id+"F31.wireOp",EDGE,"E35");
            circularPattern(context, id + "F32", {"entities" : qUnion([Q0, Q1, Q2, Q3]), "axis" : qUnion([Q4]), "angle" : 72 * degree, "instanceCount" : round(3), "oppositeDirection" : true});
        }
        {
            var Q0;
            Q0=makeQuery(id+"F6.opPattern","COPY",FACE,{"derivedFrom":makeQuery(id+"F3.opExtrude","CAP_FACE",FACE,{"disambiguationData":[OSD([sQuery(id+"F1.wireOp",EDGE,"E2.0"),sQuery(id+"F1.wireOp",EDGE,"E2.1"),sQuery(id+"F1.wireOp",EDGE,"E2.2"),sQuery(id+"F1.wireOp",EDGE,"E2.3"),sQuery(id+"F1.wireOp",EDGE,"E2.4"),sQuery(id+"F1.wireOp",EDGE,"E2.5")])],"isStart":true}),"instanceName":"2"});
            var sketch = newSketch(context, id + "F33", { "sketchPlane" : qUnion([Q0])});
            skLineSegment(sketch, "E36", {"start": v(-4.1, 7.1) * mm, "end": v(-17.1, 29.6) * mm});
            skSolve(sketch);
        }
        {
            var Q0;
            Q0=sQuery(id+"F33.wireOp",VERTEX,"E36.end");
            var Q1;
            Q1=sQuery(id+"F33.wireOp",VERTEX,"E36.start");
            var Q2;
            Q2=sQuery(id+"F11.wireOp",VERTEX,"E16.end");
            cPlane(context, id + "F34", {"entities" : qUnion([Q0, Q1, Q2]), "cplaneType" : CPlaneType.THREE_POINT, "offset" : 150 * mm, "width" : 150 * mm, "height" : 150 * mm});
        }
        {
            var Q0;
            Q0=qCreatedBy(id+"F34.planeOp",FACE);
            var sketch = newSketch(context, id + "F35", { "sketchPlane" : qUnion([Q0])});
            skLineSegment(sketch, "E37.0", {"start": v(10.32, 0) * mm, "end": v(30.97, -15.77) * mm});
            skLineSegment(sketch, "E38", {"start": v(20.65, -7.89) * mm, "end": v(38.57, 15.58) * mm});
            skSolve(sketch);
        }
        {
            var Q0;
            Q0=makeQuery(id+"F2.opExtrude","SWEPT_BODY",BODY,{"disambiguationData":[OSD([sQuery(id+"F0.wireOp",EDGE,"E0.0"),sQuery(id+"F0.wireOp",EDGE,"E0.1"),sQuery(id+"F0.wireOp",EDGE,"E0.2"),sQuery(id+"F0.wireOp",EDGE,"E0.3"),sQuery(id+"F0.wireOp",EDGE,"E0.4")])]});
            var Q1;
            Q1=sQuery(id+"F35.wireOp",EDGE,"E38");
            circularPattern(context, id + "F36", {"entities" : qUnion([Q0]), "axis" : qUnion([Q1]), "angle" : 120 * degree, "instanceCount" : round(3), "oppositeDirection" : true});
        }
        {
            var Q0;
            Q0=makeQuery(id+"F36.opPattern","COPY",FACE,{"derivedFrom":makeQuery(id+"F2.opExtrude","CAP_FACE",FACE,{"disambiguationData":[OSD([sQuery(id+"F0.wireOp",EDGE,"E0.0"),sQuery(id+"F0.wireOp",EDGE,"E0.1"),sQuery(id+"F0.wireOp",EDGE,"E0.2"),sQuery(id+"F0.wireOp",EDGE,"E0.3"),sQuery(id+"F0.wireOp",EDGE,"E0.4")])],"isStart":true}),"instanceName":"1"});
            var sketch = newSketch(context, id + "F37", { "sketchPlane" : qUnion([Q0])});
            skLineSegment(sketch, "E39", {"start": v(-4.5, -30.9) * mm, "end": v(1.45, -42.2) * mm});
            skPoint(sketch, "E40.orphan", {"position": v(-9.3, -21.76) * mm});
            skSolve(sketch);
        }
        {
            var Q0;
            Q0=sQuery(id+"F37.wireOp",VERTEX,"E39.end");
            var Q1;
            Q1=sQuery(id+"F37.wireOp",VERTEX,"E39.start");
            var Q2;
            Q2=sQuery(id+"F35.wireOp",VERTEX,"E38.end");
            cPlane(context, id + "F38", {"entities" : qUnion([Q0, Q1, Q2]), "cplaneType" : CPlaneType.THREE_POINT, "offset" : 150 * mm, "width" : 150 * mm, "height" : 150 * mm});
        }
        {
            var Q0;
            Q0=qCreatedBy(id+"F38.planeOp",FACE);
            var sketch = newSketch(context, id + "F39", { "sketchPlane" : qUnion([Q0])});
            skLineSegment(sketch, "E41.0", {"start": v(29.7, -11.34) * mm, "end": v(36.4, -22.2) * mm});
            skLineSegment(sketch, "E42", {"start": v(29.7, -11.34) * mm, "end": v(58.3, 6.33) * mm});
            skSolve(sketch);
        }
        {
            var Q0;
            Q0=makeQuery(id+"F22.opPattern","COPY",BODY,{"derivedFrom":makeQuery(id+"F17.opPattern","COPY",BODY,{"derivedFrom":makeQuery(id+"F3.opExtrude","SWEPT_BODY",BODY,{"disambiguationData":[OSD([sQuery(id+"F1.wireOp",EDGE,"E2.0"),sQuery(id+"F1.wireOp",EDGE,"E2.1"),sQuery(id+"F1.wireOp",EDGE,"E2.2"),sQuery(id+"F1.wireOp",EDGE,"E2.3"),sQuery(id+"F1.wireOp",EDGE,"E2.4"),sQuery(id+"F1.wireOp",EDGE,"E2.5")])]}),"instanceName":"1"}),"instanceName":"2"});
            var Q1;
            Q1=makeQuery(id+"F22.opPattern","COPY",BODY,{"derivedFrom":makeQuery(id+"F17.opPattern","COPY",BODY,{"derivedFrom":makeQuery(id+"F16.opPattern","COPY",BODY,{"derivedFrom":makeQuery(id+"F15.opPattern","COPY",BODY,{"derivedFrom":makeQuery(id+"F9.opExtrude","SWEPT_BODY",BODY,{"disambiguationData":[OSD([sQuery(id+"F8.wireOp",EDGE,"E7.0"),sQuery(id+"F8.wireOp",EDGE,"E10"),sQuery(id+"F8.wireOp",EDGE,"E11"),sQuery(id+"F8.wireOp",EDGE,"E12.1.0"),sQuery(id+"F8.wireOp",EDGE,"E12.1.1"),sQuery(id+"F8.wireOp",EDGE,"E12.2.0"),sQuery(id+"F8.wireOp",EDGE,"E12.2.1"),sQuery(id+"F8.wireOp",EDGE,"E12.3.0"),sQuery(id+"F8.wireOp",EDGE,"E12.3.1"),sQuery(id+"F8.wireOp",EDGE,"E12.4.0"),sQuery(id+"F8.wireOp",EDGE,"E12.4.1"),sQuery(id+"F8.wireOp",EDGE,"E12.5.0"),sQuery(id+"F8.wireOp",EDGE,"E12.5.1"),sQuery(id+"F8.wireOp",EDGE,"E12.6.0"),sQuery(id+"F8.wireOp",EDGE,"E13"),sQuery(id+"F8.wireOp",EDGE,"E14")])]}),"instanceName":"2"}),"instanceName":"1"}),"instanceName":"1"}),"instanceName":"2"});
            var Q2;
            Q2=makeQuery(id+"F22.opPattern","COPY",BODY,{"derivedFrom":makeQuery(id+"F17.opPattern","COPY",BODY,{"derivedFrom":makeQuery(id+"F13.opPattern","COPY",BODY,{"derivedFrom":makeQuery(id+"F9.opExtrude","SWEPT_BODY",BODY,{"disambiguationData":[OSD([sQuery(id+"F8.wireOp",EDGE,"E7.0"),sQuery(id+"F8.wireOp",EDGE,"E10"),sQuery(id+"F8.wireOp",EDGE,"E11"),sQuery(id+"F8.wireOp",EDGE,"E12.1.0"),sQuery(id+"F8.wireOp",EDGE,"E12.1.1"),sQuery(id+"F8.wireOp",EDGE,"E12.2.0"),sQuery(id+"F8.wireOp",EDGE,"E12.2.1"),sQuery(id+"F8.wireOp",EDGE,"E12.3.0"),sQuery(id+"F8.wireOp",EDGE,"E12.3.1"),sQuery(id+"F8.wireOp",EDGE,"E12.4.0"),sQuery(id+"F8.wireOp",EDGE,"E12.4.1"),sQuery(id+"F8.wireOp",EDGE,"E12.5.0"),sQuery(id+"F8.wireOp",EDGE,"E12.5.1"),sQuery(id+"F8.wireOp",EDGE,"E12.6.0"),sQuery(id+"F8.wireOp",EDGE,"E13"),sQuery(id+"F8.wireOp",EDGE,"E14")])]}),"instanceName":"1"}),"instanceName":"1"}),"instanceName":"2"});
            var Q3;
            Q3=makeQuery(id+"F18.opPattern","COPY",BODY,{"derivedFrom":makeQuery(id+"F13.opPattern","COPY",BODY,{"derivedFrom":makeQuery(id+"F9.opExtrude","SWEPT_BODY",BODY,{"disambiguationData":[OSD([sQuery(id+"F8.wireOp",EDGE,"E7.0"),sQuery(id+"F8.wireOp",EDGE,"E10"),sQuery(id+"F8.wireOp",EDGE,"E11"),sQuery(id+"F8.wireOp",EDGE,"E12.1.0"),sQuery(id+"F8.wireOp",EDGE,"E12.1.1"),sQuery(id+"F8.wireOp",EDGE,"E12.2.0"),sQuery(id+"F8.wireOp",EDGE,"E12.2.1"),sQuery(id+"F8.wireOp",EDGE,"E12.3.0"),sQuery(id+"F8.wireOp",EDGE,"E12.3.1"),sQuery(id+"F8.wireOp",EDGE,"E12.4.0"),sQuery(id+"F8.wireOp",EDGE,"E12.4.1"),sQuery(id+"F8.wireOp",EDGE,"E12.5.0"),sQuery(id+"F8.wireOp",EDGE,"E12.5.1"),sQuery(id+"F8.wireOp",EDGE,"E12.6.0"),sQuery(id+"F8.wireOp",EDGE,"E13"),sQuery(id+"F8.wireOp",EDGE,"E14")])]}),"instanceName":"2"}),"instanceName":"1"});
            var Q4;
            Q4=sQuery(id+"F39.wireOp",EDGE,"E42");
            circularPattern(context, id + "F40", {"entities" : qUnion([Q0, Q1, Q2, Q3]), "axis" : qUnion([Q4]), "angle" : 72 * degree, "instanceCount" : round(3), "oppositeDirection" : true});
        }
        {
            var Q0;
            Q0=makeQuery(id+"F36.opPattern","COPY",FACE,{"derivedFrom":makeQuery(id+"F2.opExtrude","CAP_FACE",FACE,{"disambiguationData":[OSD([sQuery(id+"F0.wireOp",EDGE,"E0.0"),sQuery(id+"F0.wireOp",EDGE,"E0.1"),sQuery(id+"F0.wireOp",EDGE,"E0.2"),sQuery(id+"F0.wireOp",EDGE,"E0.3"),sQuery(id+"F0.wireOp",EDGE,"E0.4")])],"isStart":true}),"instanceName":"2"});
            var sketch = newSketch(context, id + "F41", { "sketchPlane" : qUnion([Q0])});
            skLineSegment(sketch, "E43", {"start": v(0, -18.47) * mm, "end": v(0, -31.23) * mm});
            skPoint(sketch, "E44.orphan", {"position": v(0, -41.55) * mm});
            skSolve(sketch);
        }
        {
            var Q0;
            Q0=sQuery(id+"F41.wireOp",VERTEX,"E43.end");
            var Q1;
            Q1=sQuery(id+"F41.wireOp",VERTEX,"E43.start");
            var Q2;
            Q2=sQuery(id+"F11.wireOp",VERTEX,"E16.end");
            cPlane(context, id + "F42", {"entities" : qUnion([Q0, Q1, Q2]), "cplaneType" : CPlaneType.THREE_POINT, "offset" : 150 * mm, "width" : 150 * mm, "height" : 150 * mm});
        }
        {
            var Q0;
            Q0=qCreatedBy(id+"F42.planeOp",FACE);
            var sketch = newSketch(context, id + "F43", { "sketchPlane" : qUnion([Q0])});
            skLineSegment(sketch, "E45.0", {"start": v(-25.52, -7.89) * mm, "end": v(-31.23, -19.3) * mm});
            skLineSegment(sketch, "E46", {"start": v(-31.23, -19.3) * mm, "end": v(-78.41, 4.3) * mm});
            skSolve(sketch);
        }
        {
            var Q0;
            Q0=makeQuery(id+"F40.opPattern","COPY",BODY,{"derivedFrom":makeQuery(id+"F22.opPattern","COPY",BODY,{"derivedFrom":makeQuery(id+"F17.opPattern","COPY",BODY,{"derivedFrom":makeQuery(id+"F3.opExtrude","SWEPT_BODY",BODY,{"disambiguationData":[OSD([sQuery(id+"F1.wireOp",EDGE,"E2.0"),sQuery(id+"F1.wireOp",EDGE,"E2.1"),sQuery(id+"F1.wireOp",EDGE,"E2.2"),sQuery(id+"F1.wireOp",EDGE,"E2.3"),sQuery(id+"F1.wireOp",EDGE,"E2.4"),sQuery(id+"F1.wireOp",EDGE,"E2.5")])]}),"instanceName":"1"}),"instanceName":"2"}),"instanceName":"2"});
            var Q1;
            Q1=makeQuery(id+"F40.opPattern","COPY",BODY,{"derivedFrom":makeQuery(id+"F22.opPattern","COPY",BODY,{"derivedFrom":makeQuery(id+"F17.opPattern","COPY",BODY,{"derivedFrom":makeQuery(id+"F13.opPattern","COPY",BODY,{"derivedFrom":makeQuery(id+"F9.opExtrude","SWEPT_BODY",BODY,{"disambiguationData":[OSD([sQuery(id+"F8.wireOp",EDGE,"E7.0"),sQuery(id+"F8.wireOp",EDGE,"E10"),sQuery(id+"F8.wireOp",EDGE,"E11"),sQuery(id+"F8.wireOp",EDGE,"E12.1.0"),sQuery(id+"F8.wireOp",EDGE,"E12.1.1"),sQuery(id+"F8.wireOp",EDGE,"E12.2.0"),sQuery(id+"F8.wireOp",EDGE,"E12.2.1"),sQuery(id+"F8.wireOp",EDGE,"E12.3.0"),sQuery(id+"F8.wireOp",EDGE,"E12.3.1"),sQuery(id+"F8.wireOp",EDGE,"E12.4.0"),sQuery(id+"F8.wireOp",EDGE,"E12.4.1"),sQuery(id+"F8.wireOp",EDGE,"E12.5.0"),sQuery(id+"F8.wireOp",EDGE,"E12.5.1"),sQuery(id+"F8.wireOp",EDGE,"E12.6.0"),sQuery(id+"F8.wireOp",EDGE,"E13"),sQuery(id+"F8.wireOp",EDGE,"E14")])]}),"instanceName":"1"}),"instanceName":"1"}),"instanceName":"2"}),"instanceName":"2"});
            var Q2;
            Q2=makeQuery(id+"F40.opPattern","COPY",BODY,{"derivedFrom":makeQuery(id+"F18.opPattern","COPY",BODY,{"derivedFrom":makeQuery(id+"F13.opPattern","COPY",BODY,{"derivedFrom":makeQuery(id+"F9.opExtrude","SWEPT_BODY",BODY,{"disambiguationData":[OSD([sQuery(id+"F8.wireOp",EDGE,"E7.0"),sQuery(id+"F8.wireOp",EDGE,"E10"),sQuery(id+"F8.wireOp",EDGE,"E11"),sQuery(id+"F8.wireOp",EDGE,"E12.1.0"),sQuery(id+"F8.wireOp",EDGE,"E12.1.1"),sQuery(id+"F8.wireOp",EDGE,"E12.2.0"),sQuery(id+"F8.wireOp",EDGE,"E12.2.1"),sQuery(id+"F8.wireOp",EDGE,"E12.3.0"),sQuery(id+"F8.wireOp",EDGE,"E12.3.1"),sQuery(id+"F8.wireOp",EDGE,"E12.4.0"),sQuery(id+"F8.wireOp",EDGE,"E12.4.1"),sQuery(id+"F8.wireOp",EDGE,"E12.5.0"),sQuery(id+"F8.wireOp",EDGE,"E12.5.1"),sQuery(id+"F8.wireOp",EDGE,"E12.6.0"),sQuery(id+"F8.wireOp",EDGE,"E13"),sQuery(id+"F8.wireOp",EDGE,"E14")])]}),"instanceName":"2"}),"instanceName":"1"}),"instanceName":"2"});
            var Q3;
            Q3=makeQuery(id+"F40.opPattern","COPY",BODY,{"derivedFrom":makeQuery(id+"F22.opPattern","COPY",BODY,{"derivedFrom":makeQuery(id+"F17.opPattern","COPY",BODY,{"derivedFrom":makeQuery(id+"F16.opPattern","COPY",BODY,{"derivedFrom":makeQuery(id+"F15.opPattern","COPY",BODY,{"derivedFrom":makeQuery(id+"F9.opExtrude","SWEPT_BODY",BODY,{"disambiguationData":[OSD([sQuery(id+"F8.wireOp",EDGE,"E7.0"),sQuery(id+"F8.wireOp",EDGE,"E10"),sQuery(id+"F8.wireOp",EDGE,"E11"),sQuery(id+"F8.wireOp",EDGE,"E12.1.0"),sQuery(id+"F8.wireOp",EDGE,"E12.1.1"),sQuery(id+"F8.wireOp",EDGE,"E12.2.0"),sQuery(id+"F8.wireOp",EDGE,"E12.2.1"),sQuery(id+"F8.wireOp",EDGE,"E12.3.0"),sQuery(id+"F8.wireOp",EDGE,"E12.3.1"),sQuery(id+"F8.wireOp",EDGE,"E12.4.0"),sQuery(id+"F8.wireOp",EDGE,"E12.4.1"),sQuery(id+"F8.wireOp",EDGE,"E12.5.0"),sQuery(id+"F8.wireOp",EDGE,"E12.5.1"),sQuery(id+"F8.wireOp",EDGE,"E12.6.0"),sQuery(id+"F8.wireOp",EDGE,"E13"),sQuery(id+"F8.wireOp",EDGE,"E14")])]}),"instanceName":"2"}),"instanceName":"1"}),"instanceName":"1"}),"instanceName":"2"}),"instanceName":"2"});
            var Q4;
            Q4=sQuery(id+"F43.wireOp",EDGE,"E46");
            circularPattern(context, id + "F44", {"entities" : qUnion([Q0, Q1, Q2, Q3]), "axis" : qUnion([Q4]), "angle" : 72 * degree, "instanceCount" : round(3), "oppositeDirection" : true});
        }
        {
            var Q0;
            Q0=makeQuery(id+"F40.opPattern","COPY",FACE,{"derivedFrom":makeQuery(id+"F22.opPattern","COPY",FACE,{"derivedFrom":makeQuery(id+"F17.opPattern","COPY",FACE,{"derivedFrom":makeQuery(id+"F3.opExtrude","CAP_FACE",FACE,{"disambiguationData":[OSD([sQuery(id+"F1.wireOp",EDGE,"E2.0"),sQuery(id+"F1.wireOp",EDGE,"E2.1"),sQuery(id+"F1.wireOp",EDGE,"E2.2"),sQuery(id+"F1.wireOp",EDGE,"E2.3"),sQuery(id+"F1.wireOp",EDGE,"E2.4"),sQuery(id+"F1.wireOp",EDGE,"E2.5")])],"isStart":true}),"instanceName":"1"}),"instanceName":"2"}),"instanceName":"1"});
            var sketch = newSketch(context, id + "F45", { "sketchPlane" : qUnion([Q0])});
            skLineSegment(sketch, "E47", {"start": v(1.3, -21.26) * mm, "end": v(2.09, -34.23) * mm});
            skSolve(sketch);
        }
        {
            var Q0;
            Q0=sQuery(id+"F45.wireOp",VERTEX,"E47.end");
            var Q1;
            Q1=sQuery(id+"F45.wireOp",VERTEX,"E47.start");
            var Q2;
            Q2=makeQuery(id+"F6.opPattern","COPY",VERTEX,{"derivedFrom":makeQuery(id+"F3.opExtrude","CAP_VERTEX",VERTEX,{"disambiguationData":[OSD([sQuery(id+"F1.wireOp",EDGE,"E2.1"),sQuery(id+"F1.wireOp",EDGE,"E2.2")])],"isStart":true}),"instanceName":"3"});
            cPlane(context, id + "F46", {"entities" : qUnion([Q0, Q1, Q2]), "cplaneType" : CPlaneType.THREE_POINT, "offset" : 150 * mm, "width" : 150 * mm, "height" : 150 * mm});
        }
        {
            var Q0;
            Q0=qCreatedBy(id+"F46.planeOp",FACE);
            var sketch = newSketch(context, id + "F47", { "sketchPlane" : qUnion([Q0])});
            skLineSegment(sketch, "E48.0", {"start": v(-35.84, -28.53) * mm, "end": v(-33.4, -41.3) * mm});
            skLineSegment(sketch, "E49", {"start": v(-33.4, -41.3) * mm, "end": v(-61.9, -46.73) * mm});
            skSolve(sketch);
        }
        {
            var Q0;
            Q0=makeQuery(id+"F22.opPattern","COPY",BODY,{"derivedFrom":makeQuery(id+"F17.opPattern","COPY",BODY,{"derivedFrom":makeQuery(id+"F3.opExtrude","SWEPT_BODY",BODY,{"disambiguationData":[OSD([sQuery(id+"F1.wireOp",EDGE,"E2.0"),sQuery(id+"F1.wireOp",EDGE,"E2.1"),sQuery(id+"F1.wireOp",EDGE,"E2.2"),sQuery(id+"F1.wireOp",EDGE,"E2.3"),sQuery(id+"F1.wireOp",EDGE,"E2.4"),sQuery(id+"F1.wireOp",EDGE,"E2.5")])]}),"instanceName":"1"}),"instanceName":"2"});
            var Q1;
            Q1=makeQuery(id+"F22.opPattern","COPY",BODY,{"derivedFrom":makeQuery(id+"F17.opPattern","COPY",BODY,{"derivedFrom":makeQuery(id+"F13.opPattern","COPY",BODY,{"derivedFrom":makeQuery(id+"F9.opExtrude","SWEPT_BODY",BODY,{"disambiguationData":[OSD([sQuery(id+"F8.wireOp",EDGE,"E7.0"),sQuery(id+"F8.wireOp",EDGE,"E10"),sQuery(id+"F8.wireOp",EDGE,"E11"),sQuery(id+"F8.wireOp",EDGE,"E12.1.0"),sQuery(id+"F8.wireOp",EDGE,"E12.1.1"),sQuery(id+"F8.wireOp",EDGE,"E12.2.0"),sQuery(id+"F8.wireOp",EDGE,"E12.2.1"),sQuery(id+"F8.wireOp",EDGE,"E12.3.0"),sQuery(id+"F8.wireOp",EDGE,"E12.3.1"),sQuery(id+"F8.wireOp",EDGE,"E12.4.0"),sQuery(id+"F8.wireOp",EDGE,"E12.4.1"),sQuery(id+"F8.wireOp",EDGE,"E12.5.0"),sQuery(id+"F8.wireOp",EDGE,"E12.5.1"),sQuery(id+"F8.wireOp",EDGE,"E12.6.0"),sQuery(id+"F8.wireOp",EDGE,"E13"),sQuery(id+"F8.wireOp",EDGE,"E14")])]}),"instanceName":"1"}),"instanceName":"1"}),"instanceName":"2"});
            var Q2;
            Q2=makeQuery(id+"F22.opPattern","COPY",BODY,{"derivedFrom":makeQuery(id+"F17.opPattern","COPY",BODY,{"derivedFrom":makeQuery(id+"F16.opPattern","COPY",BODY,{"derivedFrom":makeQuery(id+"F15.opPattern","COPY",BODY,{"derivedFrom":makeQuery(id+"F9.opExtrude","SWEPT_BODY",BODY,{"disambiguationData":[OSD([sQuery(id+"F8.wireOp",EDGE,"E7.0"),sQuery(id+"F8.wireOp",EDGE,"E10"),sQuery(id+"F8.wireOp",EDGE,"E11"),sQuery(id+"F8.wireOp",EDGE,"E12.1.0"),sQuery(id+"F8.wireOp",EDGE,"E12.1.1"),sQuery(id+"F8.wireOp",EDGE,"E12.2.0"),sQuery(id+"F8.wireOp",EDGE,"E12.2.1"),sQuery(id+"F8.wireOp",EDGE,"E12.3.0"),sQuery(id+"F8.wireOp",EDGE,"E12.3.1"),sQuery(id+"F8.wireOp",EDGE,"E12.4.0"),sQuery(id+"F8.wireOp",EDGE,"E12.4.1"),sQuery(id+"F8.wireOp",EDGE,"E12.5.0"),sQuery(id+"F8.wireOp",EDGE,"E12.5.1"),sQuery(id+"F8.wireOp",EDGE,"E12.6.0"),sQuery(id+"F8.wireOp",EDGE,"E13"),sQuery(id+"F8.wireOp",EDGE,"E14")])]}),"instanceName":"2"}),"instanceName":"1"}),"instanceName":"1"}),"instanceName":"2"});
            var Q3;
            Q3=makeQuery(id+"F18.opPattern","COPY",BODY,{"derivedFrom":makeQuery(id+"F13.opPattern","COPY",BODY,{"derivedFrom":makeQuery(id+"F9.opExtrude","SWEPT_BODY",BODY,{"disambiguationData":[OSD([sQuery(id+"F8.wireOp",EDGE,"E7.0"),sQuery(id+"F8.wireOp",EDGE,"E10"),sQuery(id+"F8.wireOp",EDGE,"E11"),sQuery(id+"F8.wireOp",EDGE,"E12.1.0"),sQuery(id+"F8.wireOp",EDGE,"E12.1.1"),sQuery(id+"F8.wireOp",EDGE,"E12.2.0"),sQuery(id+"F8.wireOp",EDGE,"E12.2.1"),sQuery(id+"F8.wireOp",EDGE,"E12.3.0"),sQuery(id+"F8.wireOp",EDGE,"E12.3.1"),sQuery(id+"F8.wireOp",EDGE,"E12.4.0"),sQuery(id+"F8.wireOp",EDGE,"E12.4.1"),sQuery(id+"F8.wireOp",EDGE,"E12.5.0"),sQuery(id+"F8.wireOp",EDGE,"E12.5.1"),sQuery(id+"F8.wireOp",EDGE,"E12.6.0"),sQuery(id+"F8.wireOp",EDGE,"E13"),sQuery(id+"F8.wireOp",EDGE,"E14")])]}),"instanceName":"2"}),"instanceName":"1"});
            var Q4;
            Q4=sQuery(id+"F47.wireOp",EDGE,"E49");
            circularPattern(context, id + "F48", {"entities" : qUnion([Q0, Q1, Q2, Q3]), "axis" : qUnion([Q4]), "angle" : 120 * degree, "instanceCount" : 2, "oppositeDirection" : true});
        }
        {
            var Q0;
            Q0=makeQuery(id+"F26.opPattern","COPY",FACE,{"derivedFrom":makeQuery(id+"F3.opExtrude","CAP_FACE",FACE,{"disambiguationData":[OSD([sQuery(id+"F1.wireOp",EDGE,"E2.0"),sQuery(id+"F1.wireOp",EDGE,"E2.1"),sQuery(id+"F1.wireOp",EDGE,"E2.2"),sQuery(id+"F1.wireOp",EDGE,"E2.3"),sQuery(id+"F1.wireOp",EDGE,"E2.4"),sQuery(id+"F1.wireOp",EDGE,"E2.5")])],"isStart":true}),"instanceName":"1"});
            var sketch = newSketch(context, id + "F49", { "sketchPlane" : qUnion([Q0])});
            skLineSegment(sketch, "E50", {"start": v(-12.92, -27.06) * mm, "end": v(-2.09, -34.23) * mm});
            skSolve(sketch);
        }
        {
            var Q0;
            Q0=sQuery(id+"F49.wireOp",VERTEX,"E50.end");
            var Q1;
            Q1=sQuery(id+"F49.wireOp",VERTEX,"E50.start");
            var Q2;
            Q2=makeQuery(id+"F6.opPattern","COPY",VERTEX,{"derivedFrom":makeQuery(id+"F3.opExtrude","CAP_VERTEX",VERTEX,{"disambiguationData":[OSD([sQuery(id+"F1.wireOp",EDGE,"E2.0"),sQuery(id+"F1.wireOp",EDGE,"E2.5")])],"isStart":true}),"instanceName":"4"});
            cPlane(context, id + "F50", {"entities" : qUnion([Q0, Q1, Q2]), "cplaneType" : CPlaneType.THREE_POINT, "offset" : 150 * mm, "width" : 150 * mm, "height" : 150 * mm});
        }
        {
            var Q0;
            Q0=qCreatedBy(id+"F50.planeOp",FACE);
            var sketch = newSketch(context, id + "F51", { "sketchPlane" : qUnion([Q0])});
            skLineSegment(sketch, "E51.0", {"start": v(27.14, -5.92) * mm, "end": v(31.77, 6.22) * mm});
            skLineSegment(sketch, "E52", {"start": v(31.77, 6.22) * mm, "end": v(70.56, -8.6) * mm});
            skSolve(sketch);
        }
        {
            var Q0;
            Q0=makeQuery(id+"F16.opPattern","COPY",BODY,{"derivedFrom":makeQuery(id+"F15.opPattern","COPY",BODY,{"derivedFrom":makeQuery(id+"F9.opExtrude","SWEPT_BODY",BODY,{"disambiguationData":[OSD([sQuery(id+"F8.wireOp",EDGE,"E7.0"),sQuery(id+"F8.wireOp",EDGE,"E10"),sQuery(id+"F8.wireOp",EDGE,"E11"),sQuery(id+"F8.wireOp",EDGE,"E12.1.0"),sQuery(id+"F8.wireOp",EDGE,"E12.1.1"),sQuery(id+"F8.wireOp",EDGE,"E12.2.0"),sQuery(id+"F8.wireOp",EDGE,"E12.2.1"),sQuery(id+"F8.wireOp",EDGE,"E12.3.0"),sQuery(id+"F8.wireOp",EDGE,"E12.3.1"),sQuery(id+"F8.wireOp",EDGE,"E12.4.0"),sQuery(id+"F8.wireOp",EDGE,"E12.4.1"),sQuery(id+"F8.wireOp",EDGE,"E12.5.0"),sQuery(id+"F8.wireOp",EDGE,"E12.5.1"),sQuery(id+"F8.wireOp",EDGE,"E12.6.0"),sQuery(id+"F8.wireOp",EDGE,"E13"),sQuery(id+"F8.wireOp",EDGE,"E14")])]}),"instanceName":"1"}),"instanceName":"1"});
            var Q1;
            Q1=makeQuery(id+"F13.opPattern","COPY",BODY,{"derivedFrom":makeQuery(id+"F9.opExtrude","SWEPT_BODY",BODY,{"disambiguationData":[OSD([sQuery(id+"F8.wireOp",EDGE,"E7.0"),sQuery(id+"F8.wireOp",EDGE,"E10"),sQuery(id+"F8.wireOp",EDGE,"E11"),sQuery(id+"F8.wireOp",EDGE,"E12.1.0"),sQuery(id+"F8.wireOp",EDGE,"E12.1.1"),sQuery(id+"F8.wireOp",EDGE,"E12.2.0"),sQuery(id+"F8.wireOp",EDGE,"E12.2.1"),sQuery(id+"F8.wireOp",EDGE,"E12.3.0"),sQuery(id+"F8.wireOp",EDGE,"E12.3.1"),sQuery(id+"F8.wireOp",EDGE,"E12.4.0"),sQuery(id+"F8.wireOp",EDGE,"E12.4.1"),sQuery(id+"F8.wireOp",EDGE,"E12.5.0"),sQuery(id+"F8.wireOp",EDGE,"E12.5.1"),sQuery(id+"F8.wireOp",EDGE,"E12.6.0"),sQuery(id+"F8.wireOp",EDGE,"E13"),sQuery(id+"F8.wireOp",EDGE,"E14")])]}),"instanceName":"1"});
            var Q2;
            Q2=makeQuery(id+"F16.opPattern","COPY",BODY,{"derivedFrom":makeQuery(id+"F15.opPattern","COPY",BODY,{"derivedFrom":makeQuery(id+"F9.opExtrude","SWEPT_BODY",BODY,{"disambiguationData":[OSD([sQuery(id+"F8.wireOp",EDGE,"E7.0"),sQuery(id+"F8.wireOp",EDGE,"E10"),sQuery(id+"F8.wireOp",EDGE,"E11"),sQuery(id+"F8.wireOp",EDGE,"E12.1.0"),sQuery(id+"F8.wireOp",EDGE,"E12.1.1"),sQuery(id+"F8.wireOp",EDGE,"E12.2.0"),sQuery(id+"F8.wireOp",EDGE,"E12.2.1"),sQuery(id+"F8.wireOp",EDGE,"E12.3.0"),sQuery(id+"F8.wireOp",EDGE,"E12.3.1"),sQuery(id+"F8.wireOp",EDGE,"E12.4.0"),sQuery(id+"F8.wireOp",EDGE,"E12.4.1"),sQuery(id+"F8.wireOp",EDGE,"E12.5.0"),sQuery(id+"F8.wireOp",EDGE,"E12.5.1"),sQuery(id+"F8.wireOp",EDGE,"E12.6.0"),sQuery(id+"F8.wireOp",EDGE,"E13"),sQuery(id+"F8.wireOp",EDGE,"E14")])]}),"instanceName":"2"}),"instanceName":"1"});
            var Q3;
            Q3=makeQuery(id+"F3.opExtrude","SWEPT_BODY",BODY,{"disambiguationData":[OSD([sQuery(id+"F1.wireOp",EDGE,"E2.0"),sQuery(id+"F1.wireOp",EDGE,"E2.1"),sQuery(id+"F1.wireOp",EDGE,"E2.2"),sQuery(id+"F1.wireOp",EDGE,"E2.3"),sQuery(id+"F1.wireOp",EDGE,"E2.4"),sQuery(id+"F1.wireOp",EDGE,"E2.5")])]});
            var Q4;
            Q4=sQuery(id+"F51.wireOp",EDGE,"E52");
            circularPattern(context, id + "F52", {"entities" : qUnion([Q0, Q1, Q2, Q3]), "axis" : qUnion([Q4]), "angle" : 120 * degree, "instanceCount" : round(2), "oppositeDirection" : true});
        }
        {
            var Q0;
            Q0=makeQuery(id+"F32.opPattern","COPY",FACE,{"derivedFrom":makeQuery(id+"F26.opPattern","COPY",FACE,{"derivedFrom":makeQuery(id+"F3.opExtrude","CAP_FACE",FACE,{"disambiguationData":[OSD([sQuery(id+"F1.wireOp",EDGE,"E2.0"),sQuery(id+"F1.wireOp",EDGE,"E2.1"),sQuery(id+"F1.wireOp",EDGE,"E2.2"),sQuery(id+"F1.wireOp",EDGE,"E2.3"),sQuery(id+"F1.wireOp",EDGE,"E2.4"),sQuery(id+"F1.wireOp",EDGE,"E2.5")])],"isStart":true}),"instanceName":"2"}),"instanceName":"1"});
            var sketch = newSketch(context, id + "F53", { "sketchPlane" : qUnion([Q0])});
            skLineSegment(sketch, "E53", {"start": v(-10.6, -33.35) * mm, "end": v(-10.6, -18.35) * mm});
            skSolve(sketch);
        }
        {
            var Q0;
            Q0=sQuery(id+"F53.wireOp",VERTEX,"E53.start");
            var Q1;
            Q1=sQuery(id+"F53.wireOp",VERTEX,"E53.end");
            var Q2;
            Q2=makeQuery(id+"F32.opPattern","COPY",VERTEX,{"derivedFrom":makeQuery(id+"F26.opPattern","COPY",VERTEX,{"derivedFrom":makeQuery(id+"F3.opExtrude","CAP_VERTEX",VERTEX,{"disambiguationData":[OSD([sQuery(id+"F1.wireOp",EDGE,"E2.2"),sQuery(id+"F1.wireOp",EDGE,"E2.3")])],"isStart":false}),"instanceName":"2"}),"instanceName":"1"});
            cPlane(context, id + "F54", {"entities" : qUnion([Q0, Q1, Q2]), "cplaneType" : CPlaneType.THREE_POINT, "offset" : 150 * mm, "width" : 150 * mm, "height" : 150 * mm});
        }
        {
            var Q0;
            Q0=qCreatedBy(id+"F54.planeOp",FACE);
            var sketch = newSketch(context, id + "F55", { "sketchPlane" : qUnion([Q0])});
            skLineSegment(sketch, "E54.0", {"start": v(-2, -70.16) * mm, "end": v(-14.98, -62.66) * mm});
            skLineSegment(sketch, "E55", {"start": v(-14.98, -62.66) * mm, "end": v(-37.7, -102) * mm});
            skSolve(sketch);
        }
        {
            var Q0;
            Q0=makeQuery(id+"F26.opPattern","COPY",BODY,{"derivedFrom":makeQuery(id+"F3.opExtrude","SWEPT_BODY",BODY,{"disambiguationData":[OSD([sQuery(id+"F1.wireOp",EDGE,"E2.0"),sQuery(id+"F1.wireOp",EDGE,"E2.1"),sQuery(id+"F1.wireOp",EDGE,"E2.2"),sQuery(id+"F1.wireOp",EDGE,"E2.3"),sQuery(id+"F1.wireOp",EDGE,"E2.4"),sQuery(id+"F1.wireOp",EDGE,"E2.5")])]}),"instanceName":"2"});
            var Q1;
            Q1=makeQuery(id+"F26.opPattern","COPY",BODY,{"derivedFrom":makeQuery(id+"F16.opPattern","COPY",BODY,{"derivedFrom":makeQuery(id+"F15.opPattern","COPY",BODY,{"derivedFrom":makeQuery(id+"F9.opExtrude","SWEPT_BODY",BODY,{"disambiguationData":[OSD([sQuery(id+"F8.wireOp",EDGE,"E7.0"),sQuery(id+"F8.wireOp",EDGE,"E10"),sQuery(id+"F8.wireOp",EDGE,"E11"),sQuery(id+"F8.wireOp",EDGE,"E12.1.0"),sQuery(id+"F8.wireOp",EDGE,"E12.1.1"),sQuery(id+"F8.wireOp",EDGE,"E12.2.0"),sQuery(id+"F8.wireOp",EDGE,"E12.2.1"),sQuery(id+"F8.wireOp",EDGE,"E12.3.0"),sQuery(id+"F8.wireOp",EDGE,"E12.3.1"),sQuery(id+"F8.wireOp",EDGE,"E12.4.0"),sQuery(id+"F8.wireOp",EDGE,"E12.4.1"),sQuery(id+"F8.wireOp",EDGE,"E12.5.0"),sQuery(id+"F8.wireOp",EDGE,"E12.5.1"),sQuery(id+"F8.wireOp",EDGE,"E12.6.0"),sQuery(id+"F8.wireOp",EDGE,"E13"),sQuery(id+"F8.wireOp",EDGE,"E14")])]}),"instanceName":"2"}),"instanceName":"1"}),"instanceName":"2"});
            var Q2;
            Q2=makeQuery(id+"F26.opPattern","COPY",BODY,{"derivedFrom":makeQuery(id+"F13.opPattern","COPY",BODY,{"derivedFrom":makeQuery(id+"F9.opExtrude","SWEPT_BODY",BODY,{"disambiguationData":[OSD([sQuery(id+"F8.wireOp",EDGE,"E7.0"),sQuery(id+"F8.wireOp",EDGE,"E10"),sQuery(id+"F8.wireOp",EDGE,"E11"),sQuery(id+"F8.wireOp",EDGE,"E12.1.0"),sQuery(id+"F8.wireOp",EDGE,"E12.1.1"),sQuery(id+"F8.wireOp",EDGE,"E12.2.0"),sQuery(id+"F8.wireOp",EDGE,"E12.2.1"),sQuery(id+"F8.wireOp",EDGE,"E12.3.0"),sQuery(id+"F8.wireOp",EDGE,"E12.3.1"),sQuery(id+"F8.wireOp",EDGE,"E12.4.0"),sQuery(id+"F8.wireOp",EDGE,"E12.4.1"),sQuery(id+"F8.wireOp",EDGE,"E12.5.0"),sQuery(id+"F8.wireOp",EDGE,"E12.5.1"),sQuery(id+"F8.wireOp",EDGE,"E12.6.0"),sQuery(id+"F8.wireOp",EDGE,"E13"),sQuery(id+"F8.wireOp",EDGE,"E14")])]}),"instanceName":"1"}),"instanceName":"2"});
            var Q3;
            Q3=makeQuery(id+"F18.opPattern","COPY",BODY,{"derivedFrom":makeQuery(id+"F13.opPattern","COPY",BODY,{"derivedFrom":makeQuery(id+"F9.opExtrude","SWEPT_BODY",BODY,{"disambiguationData":[OSD([sQuery(id+"F8.wireOp",EDGE,"E7.0"),sQuery(id+"F8.wireOp",EDGE,"E10"),sQuery(id+"F8.wireOp",EDGE,"E11"),sQuery(id+"F8.wireOp",EDGE,"E12.1.0"),sQuery(id+"F8.wireOp",EDGE,"E12.1.1"),sQuery(id+"F8.wireOp",EDGE,"E12.2.0"),sQuery(id+"F8.wireOp",EDGE,"E12.2.1"),sQuery(id+"F8.wireOp",EDGE,"E12.3.0"),sQuery(id+"F8.wireOp",EDGE,"E12.3.1"),sQuery(id+"F8.wireOp",EDGE,"E12.4.0"),sQuery(id+"F8.wireOp",EDGE,"E12.4.1"),sQuery(id+"F8.wireOp",EDGE,"E12.5.0"),sQuery(id+"F8.wireOp",EDGE,"E12.5.1"),sQuery(id+"F8.wireOp",EDGE,"E12.6.0"),sQuery(id+"F8.wireOp",EDGE,"E13"),sQuery(id+"F8.wireOp",EDGE,"E14")])]}),"instanceName":"2"}),"instanceName":"2"});
            var Q4;
            Q4=sQuery(id+"F55.wireOp",EDGE,"E55");
            circularPattern(context, id + "F56", {"entities" : qUnion([Q0, Q1, Q2, Q3]), "axis" : qUnion([Q4]), "angle" : 120 * degree, "instanceCount" : 2, "oppositeDirection" : true});
        }
        {
            var Q0;
            Q0=makeQuery(id+"F56.opPattern","COPY",FACE,{"derivedFrom":makeQuery(id+"F26.opPattern","COPY",FACE,{"derivedFrom":makeQuery(id+"F3.opExtrude","CAP_FACE",FACE,{"disambiguationData":[OSD([sQuery(id+"F1.wireOp",EDGE,"E2.0"),sQuery(id+"F1.wireOp",EDGE,"E2.1"),sQuery(id+"F1.wireOp",EDGE,"E2.2"),sQuery(id+"F1.wireOp",EDGE,"E2.3"),sQuery(id+"F1.wireOp",EDGE,"E2.4"),sQuery(id+"F1.wireOp",EDGE,"E2.5")])],"isStart":true}),"instanceName":"2"}),"instanceName":"1"});
            var sketch = newSketch(context, id + "F57", { "sketchPlane" : qUnion([Q0])});
            skLineSegment(sketch, "E56", {"start": v(-34.48, 6) * mm, "end": v(-19.62, 8.02) * mm});
            skSolve(sketch);
        }
        {
            var Q0;
            Q0=sQuery(id+"F57.wireOp",VERTEX,"E56.start");
            var Q1;
            Q1=sQuery(id+"F57.wireOp",VERTEX,"E56.end");
            var Q2;
            Q2=makeQuery(id+"F56.opPattern","COPY",VERTEX,{"derivedFrom":makeQuery(id+"F26.opPattern","COPY",VERTEX,{"derivedFrom":makeQuery(id+"F3.opExtrude","CAP_VERTEX",VERTEX,{"disambiguationData":[OSD([sQuery(id+"F1.wireOp",EDGE,"E2.2"),sQuery(id+"F1.wireOp",EDGE,"E2.3")])],"isStart":false}),"instanceName":"2"}),"instanceName":"1"});
            cPlane(context, id + "F58", {"entities" : qUnion([Q0, Q1, Q2]), "cplaneType" : CPlaneType.THREE_POINT, "offset" : 150 * mm, "width" : 150 * mm, "height" : 150 * mm});
        }
        {
            var Q0;
            Q0=qCreatedBy(id+"F58.planeOp",FACE);
            var sketch = newSketch(context, id + "F59", { "sketchPlane" : qUnion([Q0])});
            skLineSegment(sketch, "E57.0", {"start": v(-8.72, -69.64) * mm, "end": v(-20.93, -60.93) * mm});
            skLineSegment(sketch, "E58", {"start": v(-20.93, -60.93) * mm, "end": v(-30.12, -73.8) * mm});
            skSolve(sketch);
        }
        {
            var Q0;
            Q0=makeQuery(id+"F52.opPattern","COPY",BODY,{"derivedFrom":makeQuery(id+"F3.opExtrude","SWEPT_BODY",BODY,{"disambiguationData":[OSD([sQuery(id+"F1.wireOp",EDGE,"E2.0"),sQuery(id+"F1.wireOp",EDGE,"E2.1"),sQuery(id+"F1.wireOp",EDGE,"E2.2"),sQuery(id+"F1.wireOp",EDGE,"E2.3"),sQuery(id+"F1.wireOp",EDGE,"E2.4"),sQuery(id+"F1.wireOp",EDGE,"E2.5")])]}),"instanceName":"1"});
            var Q1;
            Q1=makeQuery(id+"F52.opPattern","COPY",BODY,{"derivedFrom":makeQuery(id+"F16.opPattern","COPY",BODY,{"derivedFrom":makeQuery(id+"F15.opPattern","COPY",BODY,{"derivedFrom":makeQuery(id+"F9.opExtrude","SWEPT_BODY",BODY,{"disambiguationData":[OSD([sQuery(id+"F8.wireOp",EDGE,"E7.0"),sQuery(id+"F8.wireOp",EDGE,"E10"),sQuery(id+"F8.wireOp",EDGE,"E11"),sQuery(id+"F8.wireOp",EDGE,"E12.1.0"),sQuery(id+"F8.wireOp",EDGE,"E12.1.1"),sQuery(id+"F8.wireOp",EDGE,"E12.2.0"),sQuery(id+"F8.wireOp",EDGE,"E12.2.1"),sQuery(id+"F8.wireOp",EDGE,"E12.3.0"),sQuery(id+"F8.wireOp",EDGE,"E12.3.1"),sQuery(id+"F8.wireOp",EDGE,"E12.4.0"),sQuery(id+"F8.wireOp",EDGE,"E12.4.1"),sQuery(id+"F8.wireOp",EDGE,"E12.5.0"),sQuery(id+"F8.wireOp",EDGE,"E12.5.1"),sQuery(id+"F8.wireOp",EDGE,"E12.6.0"),sQuery(id+"F8.wireOp",EDGE,"E13"),sQuery(id+"F8.wireOp",EDGE,"E14")])]}),"instanceName":"2"}),"instanceName":"1"}),"instanceName":"1"});
            var Q2;
            Q2=makeQuery(id+"F52.opPattern","COPY",BODY,{"derivedFrom":makeQuery(id+"F16.opPattern","COPY",BODY,{"derivedFrom":makeQuery(id+"F15.opPattern","COPY",BODY,{"derivedFrom":makeQuery(id+"F9.opExtrude","SWEPT_BODY",BODY,{"disambiguationData":[OSD([sQuery(id+"F8.wireOp",EDGE,"E7.0"),sQuery(id+"F8.wireOp",EDGE,"E10"),sQuery(id+"F8.wireOp",EDGE,"E11"),sQuery(id+"F8.wireOp",EDGE,"E12.1.0"),sQuery(id+"F8.wireOp",EDGE,"E12.1.1"),sQuery(id+"F8.wireOp",EDGE,"E12.2.0"),sQuery(id+"F8.wireOp",EDGE,"E12.2.1"),sQuery(id+"F8.wireOp",EDGE,"E12.3.0"),sQuery(id+"F8.wireOp",EDGE,"E12.3.1"),sQuery(id+"F8.wireOp",EDGE,"E12.4.0"),sQuery(id+"F8.wireOp",EDGE,"E12.4.1"),sQuery(id+"F8.wireOp",EDGE,"E12.5.0"),sQuery(id+"F8.wireOp",EDGE,"E12.5.1"),sQuery(id+"F8.wireOp",EDGE,"E12.6.0"),sQuery(id+"F8.wireOp",EDGE,"E13"),sQuery(id+"F8.wireOp",EDGE,"E14")])]}),"instanceName":"1"}),"instanceName":"1"}),"instanceName":"1"});
            var Q3;
            Q3=makeQuery(id+"F52.opPattern","COPY",BODY,{"derivedFrom":makeQuery(id+"F13.opPattern","COPY",BODY,{"derivedFrom":makeQuery(id+"F9.opExtrude","SWEPT_BODY",BODY,{"disambiguationData":[OSD([sQuery(id+"F8.wireOp",EDGE,"E7.0"),sQuery(id+"F8.wireOp",EDGE,"E10"),sQuery(id+"F8.wireOp",EDGE,"E11"),sQuery(id+"F8.wireOp",EDGE,"E12.1.0"),sQuery(id+"F8.wireOp",EDGE,"E12.1.1"),sQuery(id+"F8.wireOp",EDGE,"E12.2.0"),sQuery(id+"F8.wireOp",EDGE,"E12.2.1"),sQuery(id+"F8.wireOp",EDGE,"E12.3.0"),sQuery(id+"F8.wireOp",EDGE,"E12.3.1"),sQuery(id+"F8.wireOp",EDGE,"E12.4.0"),sQuery(id+"F8.wireOp",EDGE,"E12.4.1"),sQuery(id+"F8.wireOp",EDGE,"E12.5.0"),sQuery(id+"F8.wireOp",EDGE,"E12.5.1"),sQuery(id+"F8.wireOp",EDGE,"E12.6.0"),sQuery(id+"F8.wireOp",EDGE,"E13"),sQuery(id+"F8.wireOp",EDGE,"E14")])]}),"instanceName":"1"}),"instanceName":"1"});
            var Q4;
            Q4=sQuery(id+"F59.wireOp",EDGE,"E58");
            circularPattern(context, id + "F60", {"entities" : qUnion([Q0, Q1, Q2, Q3]), "axis" : qUnion([Q4]), "angle" : 120 * degree, "instanceCount" : 2, "oppositeDirection" : true});
        }
        {
            var Q0;
            Q0=makeQuery(id+"F22.opPattern","COPY",BODY,{"derivedFrom":makeQuery(id+"F17.opPattern","COPY",BODY,{"derivedFrom":makeQuery(id+"F16.opPattern","COPY",BODY,{"derivedFrom":makeQuery(id+"F15.opPattern","COPY",BODY,{"derivedFrom":makeQuery(id+"F9.opExtrude","SWEPT_BODY",BODY,{"disambiguationData":[OSD([sQuery(id+"F8.wireOp",EDGE,"E7.0"),sQuery(id+"F8.wireOp",EDGE,"E10"),sQuery(id+"F8.wireOp",EDGE,"E11"),sQuery(id+"F8.wireOp",EDGE,"E12.1.0"),sQuery(id+"F8.wireOp",EDGE,"E12.1.1"),sQuery(id+"F8.wireOp",EDGE,"E12.2.0"),sQuery(id+"F8.wireOp",EDGE,"E12.2.1"),sQuery(id+"F8.wireOp",EDGE,"E12.3.0"),sQuery(id+"F8.wireOp",EDGE,"E12.3.1"),sQuery(id+"F8.wireOp",EDGE,"E12.4.0"),sQuery(id+"F8.wireOp",EDGE,"E12.4.1"),sQuery(id+"F8.wireOp",EDGE,"E12.5.0"),sQuery(id+"F8.wireOp",EDGE,"E12.5.1"),sQuery(id+"F8.wireOp",EDGE,"E12.6.0"),sQuery(id+"F8.wireOp",EDGE,"E13"),sQuery(id+"F8.wireOp",EDGE,"E14")])]}),"instanceName":"1"}),"instanceName":"1"}),"instanceName":"1"}),"instanceName":"1"});
            deleteBodies(context, id + "F61", {"entities" : qUnion([Q0])});
        }
        {
            var Q0;
            Q0=makeQuery(id+"F22.opPattern","COPY",BODY,{"derivedFrom":makeQuery(id+"F17.opPattern","COPY",BODY,{"derivedFrom":makeQuery(id+"F16.opPattern","COPY",BODY,{"derivedFrom":makeQuery(id+"F15.opPattern","COPY",BODY,{"derivedFrom":makeQuery(id+"F9.opExtrude","SWEPT_BODY",BODY,{"disambiguationData":[OSD([sQuery(id+"F8.wireOp",EDGE,"E7.0"),sQuery(id+"F8.wireOp",EDGE,"E10"),sQuery(id+"F8.wireOp",EDGE,"E11"),sQuery(id+"F8.wireOp",EDGE,"E12.1.0"),sQuery(id+"F8.wireOp",EDGE,"E12.1.1"),sQuery(id+"F8.wireOp",EDGE,"E12.2.0"),sQuery(id+"F8.wireOp",EDGE,"E12.2.1"),sQuery(id+"F8.wireOp",EDGE,"E12.3.0"),sQuery(id+"F8.wireOp",EDGE,"E12.3.1"),sQuery(id+"F8.wireOp",EDGE,"E12.4.0"),sQuery(id+"F8.wireOp",EDGE,"E12.4.1"),sQuery(id+"F8.wireOp",EDGE,"E12.5.0"),sQuery(id+"F8.wireOp",EDGE,"E12.5.1"),sQuery(id+"F8.wireOp",EDGE,"E12.6.0"),sQuery(id+"F8.wireOp",EDGE,"E13"),sQuery(id+"F8.wireOp",EDGE,"E14")])]}),"instanceName":"1"}),"instanceName":"1"}),"instanceName":"1"}),"instanceName":"2"});
            deleteBodies(context, id + "F62", {"entities" : qUnion([Q0])});
        }
        {
            var Q0;
            Q0=makeQuery(id+"F26.opPattern","COPY",BODY,{"derivedFrom":makeQuery(id+"F16.opPattern","COPY",BODY,{"derivedFrom":makeQuery(id+"F15.opPattern","COPY",BODY,{"derivedFrom":makeQuery(id+"F9.opExtrude","SWEPT_BODY",BODY,{"disambiguationData":[OSD([sQuery(id+"F8.wireOp",EDGE,"E7.0"),sQuery(id+"F8.wireOp",EDGE,"E10"),sQuery(id+"F8.wireOp",EDGE,"E11"),sQuery(id+"F8.wireOp",EDGE,"E12.1.0"),sQuery(id+"F8.wireOp",EDGE,"E12.1.1"),sQuery(id+"F8.wireOp",EDGE,"E12.2.0"),sQuery(id+"F8.wireOp",EDGE,"E12.2.1"),sQuery(id+"F8.wireOp",EDGE,"E12.3.0"),sQuery(id+"F8.wireOp",EDGE,"E12.3.1"),sQuery(id+"F8.wireOp",EDGE,"E12.4.0"),sQuery(id+"F8.wireOp",EDGE,"E12.4.1"),sQuery(id+"F8.wireOp",EDGE,"E12.5.0"),sQuery(id+"F8.wireOp",EDGE,"E12.5.1"),sQuery(id+"F8.wireOp",EDGE,"E12.6.0"),sQuery(id+"F8.wireOp",EDGE,"E13"),sQuery(id+"F8.wireOp",EDGE,"E14")])]}),"instanceName":"1"}),"instanceName":"1"}),"instanceName":"1"});
            deleteBodies(context, id + "F63", {"entities" : qUnion([Q0])});
        }
        {
            var Q0;
            Q0=makeQuery(id+"F26.opPattern","COPY",BODY,{"derivedFrom":makeQuery(id+"F16.opPattern","COPY",BODY,{"derivedFrom":makeQuery(id+"F15.opPattern","COPY",BODY,{"derivedFrom":makeQuery(id+"F9.opExtrude","SWEPT_BODY",BODY,{"disambiguationData":[OSD([sQuery(id+"F8.wireOp",EDGE,"E7.0"),sQuery(id+"F8.wireOp",EDGE,"E10"),sQuery(id+"F8.wireOp",EDGE,"E11"),sQuery(id+"F8.wireOp",EDGE,"E12.1.0"),sQuery(id+"F8.wireOp",EDGE,"E12.1.1"),sQuery(id+"F8.wireOp",EDGE,"E12.2.0"),sQuery(id+"F8.wireOp",EDGE,"E12.2.1"),sQuery(id+"F8.wireOp",EDGE,"E12.3.0"),sQuery(id+"F8.wireOp",EDGE,"E12.3.1"),sQuery(id+"F8.wireOp",EDGE,"E12.4.0"),sQuery(id+"F8.wireOp",EDGE,"E12.4.1"),sQuery(id+"F8.wireOp",EDGE,"E12.5.0"),sQuery(id+"F8.wireOp",EDGE,"E12.5.1"),sQuery(id+"F8.wireOp",EDGE,"E12.6.0"),sQuery(id+"F8.wireOp",EDGE,"E13"),sQuery(id+"F8.wireOp",EDGE,"E14")])]}),"instanceName":"1"}),"instanceName":"1"}),"instanceName":"2"});
            deleteBodies(context, id + "F64", {"entities" : qUnion([Q0])});
        }
        {
            var Q0;
            Q0 = qBodyType(qCreatedBy(id + "F1" ,EDGE), BodyType.WIRE);
            var sketch = newSketch(context, id + "F65", { "sketchPlane" : qUnion([Q0])});
            skSolve(sketch);
        }
        {
            var Q0;
            Q0 = qSketchRegion(id + "F65", true);
            var Q1;
            Q1=makeQuery(id+"F16.opPattern","COPY",FACE,{"derivedFrom":makeQuery(id+"F15.opPattern","COPY",FACE,{"derivedFrom":makeQuery(id+"F9.opExtrude","CAP_FACE",FACE,{"disambiguationData":[OSD([sQuery(id+"F8.wireOp",EDGE,"E7.0"),sQuery(id+"F8.wireOp",EDGE,"E10"),sQuery(id+"F8.wireOp",EDGE,"E11"),sQuery(id+"F8.wireOp",EDGE,"E12.1.0"),sQuery(id+"F8.wireOp",EDGE,"E12.1.1"),sQuery(id+"F8.wireOp",EDGE,"E12.2.0"),sQuery(id+"F8.wireOp",EDGE,"E12.2.1"),sQuery(id+"F8.wireOp",EDGE,"E12.3.0"),sQuery(id+"F8.wireOp",EDGE,"E12.3.1"),sQuery(id+"F8.wireOp",EDGE,"E12.4.0"),sQuery(id+"F8.wireOp",EDGE,"E12.4.1"),sQuery(id+"F8.wireOp",EDGE,"E12.5.0"),sQuery(id+"F8.wireOp",EDGE,"E12.5.1"),sQuery(id+"F8.wireOp",EDGE,"E12.6.0"),sQuery(id+"F8.wireOp",EDGE,"E13"),sQuery(id+"F8.wireOp",EDGE,"E14")])],"isStart":true}),"instanceName":"2"}),"instanceName":"2"});
            extrude(context, id + "F66", {"entities" : qUnion([Q0, Q1]), "depth" : 25 * mm});
        }
    });
